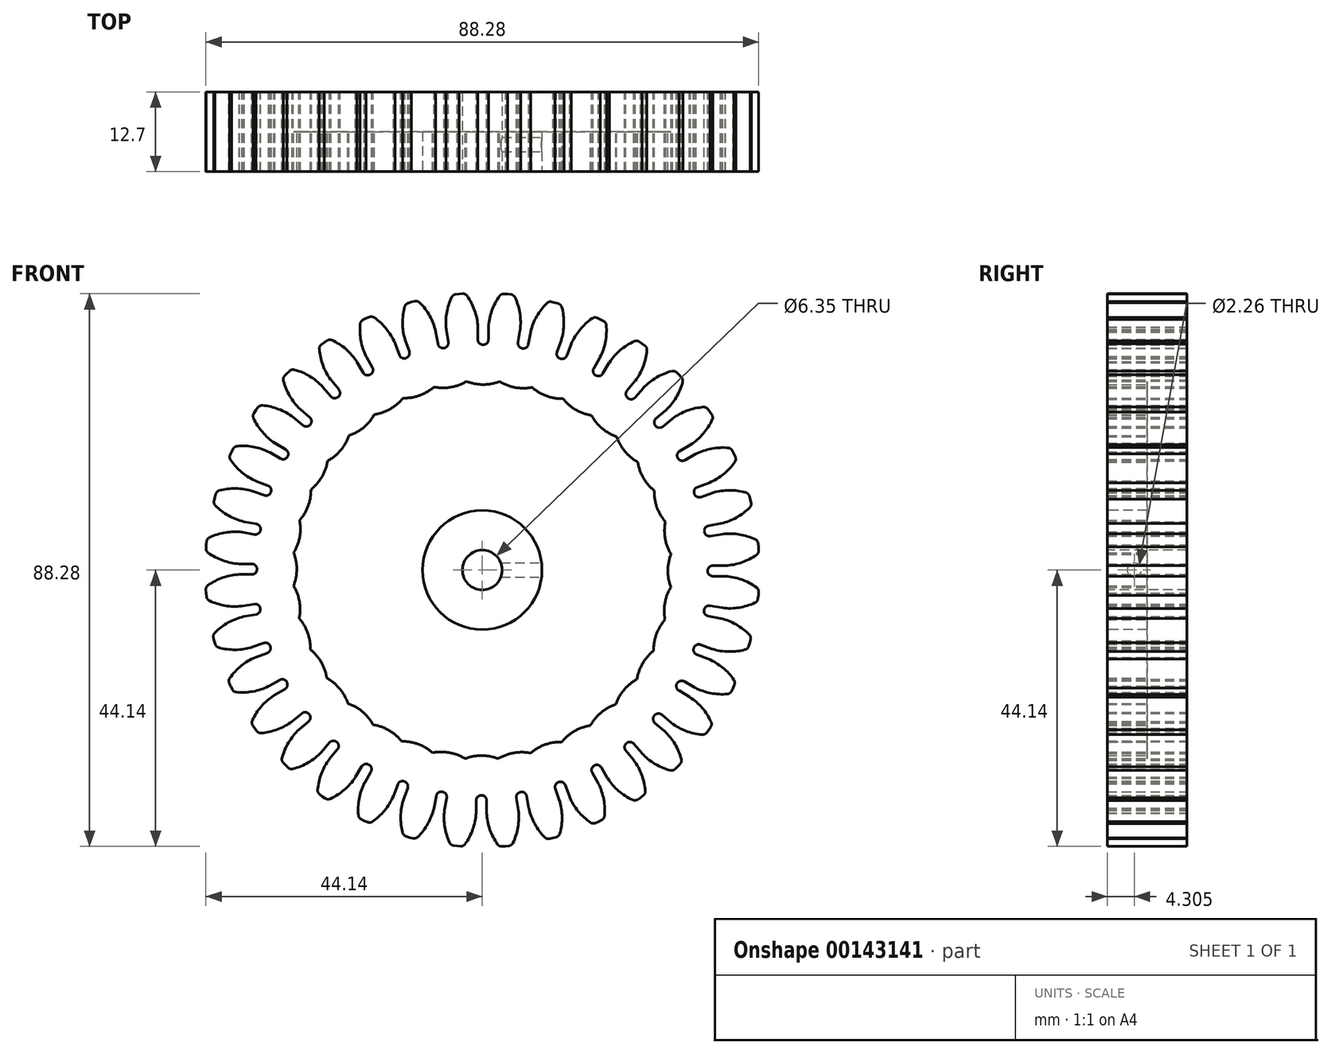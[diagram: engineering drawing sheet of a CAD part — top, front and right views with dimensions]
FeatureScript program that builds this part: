
annotation { "Feature Type Name" : "Feature", "Feature Type Description" : "" }
export const myFeature = defineFeature(function(context is Context, id is Id, definition is map)
    precondition{}
    {
        {
            var Q0;
            Q0=qCreatedBy(makeId("Front.planeOp"),FACE);
            var sketch = newSketch(context, id + "F0", { "sketchPlane" : qUnion([Q0])});
            skArc(sketch, "E0.trimOffspring", {"start": v(-0.7, 38.83) * mm, "mid": v(-1.22, 41.43) * mm, "end": v(-2.42, 43.78) * mm});
            skLineSegment(sketch, "E1", {"start": v(-3.13, 44.14) * mm, "end": v(-3.7, 44.11) * mm});
            skLineSegment(sketch, "E2", {"start": v(-0.7, 38.79) * mm, "end": v(-0.7, 36.8) * mm});
            skArc(sketch, "E3.filletArc", {"start": v(-0.7, 36.8) * mm, "mid": v(-0.46, 36.22) * mm, "end": v(0.12, 35.98) * mm});
            skArc(sketch, "E4.filletArc", {"start": v(-2.42, 43.78) * mm, "mid": v(-2.73, 44.05) * mm, "end": v(-3.13, 44.14) * mm});
            skArc(sketch, "E5.filletArc", {"start": v(-0.7, 38.79) * mm, "mid": v(-0.7, 38.8) * mm, "end": v(-0.7, 38.83) * mm});
            skLineSegment(sketch, "E6.MirrorCS", {"start": v(-4.25, 44.04) * mm, "end": v(-3.7, 44.11) * mm});
            skArc(sketch, "E7.MirrorCS", {"start": v(-4.9, 43.58) * mm, "mid": v(-4.63, 43.9) * mm, "end": v(-4.25, 44.04) * mm});
            skArc(sketch, "E8.MirrorCS", {"start": v(-5.76, 38.4) * mm, "mid": v(-5.69, 41.05) * mm, "end": v(-4.9, 43.58) * mm});
            skLineSegment(sketch, "E9.MirrorCS", {"start": v(-5.75, 38.36) * mm, "end": v(-5.42, 36.4) * mm});
            skArc(sketch, "E10.MirrorCS", {"start": v(-5.42, 36.4) * mm, "mid": v(-5.56, 35.8) * mm, "end": v(-6.1, 35.46) * mm});
            skArc(sketch, "E11.1.0", {"start": v(-11.66, 34.91) * mm, "mid": v(-11.7, 34.28) * mm, "end": v(-12.16, 33.86) * mm});
            skLineSegment(sketch, "E11.1.1", {"start": v(-12.33, 36.78) * mm, "end": v(-11.66, 34.91) * mm});
            skArc(sketch, "E11.1.2", {"start": v(-12.34, 36.82) * mm, "mid": v(-12.73, 39.44) * mm, "end": v(-12.39, 42.07) * mm});
            skArc(sketch, "E11.1.3", {"start": v(-12.39, 42.07) * mm, "mid": v(-12.18, 42.42) * mm, "end": v(-11.83, 42.63) * mm});
            skLineSegment(sketch, "E11.1.4", {"start": v(-11.83, 42.63) * mm, "end": v(-11.3, 42.8) * mm});
            skLineSegment(sketch, "E11.1.5", {"start": v(-10.75, 42.92) * mm, "end": v(-11.3, 42.8) * mm});
            skArc(sketch, "E11.1.6", {"start": v(-9.99, 42.7) * mm, "mid": v(-10.34, 42.9) * mm, "end": v(-10.75, 42.92) * mm});
            skArc(sketch, "E11.1.7", {"start": v(-7.44, 38.12) * mm, "mid": v(-8.4, 40.59) * mm, "end": v(-9.99, 42.7) * mm});
            skLineSegment(sketch, "E11.1.8", {"start": v(-7.43, 38.07) * mm, "end": v(-7.09, 36.12) * mm});
            skArc(sketch, "E11.1.9", {"start": v(-7.09, 36.12) * mm, "mid": v(-6.75, 35.6) * mm, "end": v(-6.13, 35.45) * mm});
            skArc(sketch, "E11.2.0", {"start": v(-17.55, 32.36) * mm, "mid": v(-17.47, 31.73) * mm, "end": v(-17.86, 31.23) * mm});
            skLineSegment(sketch, "E11.2.1", {"start": v(-18.53, 34.08) * mm, "end": v(-17.55, 32.36) * mm});
            skArc(sketch, "E11.2.2", {"start": v(-18.55, 34.12) * mm, "mid": v(-19.39, 36.63) * mm, "end": v(-19.5, 39.28) * mm});
            skArc(sketch, "E11.2.3", {"start": v(-19.5, 39.28) * mm, "mid": v(-19.36, 39.66) * mm, "end": v(-19.06, 39.93) * mm});
            skLineSegment(sketch, "E11.2.4", {"start": v(-19.06, 39.93) * mm, "end": v(-18.56, 40.19) * mm});
            skLineSegment(sketch, "E11.2.5", {"start": v(-18.04, 40.4) * mm, "end": v(-18.56, 40.19) * mm});
            skArc(sketch, "E11.2.6", {"start": v(-17.25, 40.32) * mm, "mid": v(-17.63, 40.46) * mm, "end": v(-18.04, 40.4) * mm});
            skArc(sketch, "E11.2.7", {"start": v(-13.95, 36.25) * mm, "mid": v(-15.31, 38.51) * mm, "end": v(-17.25, 40.32) * mm});
            skLineSegment(sketch, "E11.2.8", {"start": v(-13.93, 36.2) * mm, "end": v(-13.25, 34.34) * mm});
            skArc(sketch, "E11.2.9", {"start": v(-13.25, 34.34) * mm, "mid": v(-12.83, 33.88) * mm, "end": v(-12.2, 33.85) * mm});
            skArc(sketch, "E11.3.0", {"start": v(-22.9, 28.82) * mm, "mid": v(-22.72, 28.22) * mm, "end": v(-23.01, 27.66) * mm});
            skLineSegment(sketch, "E11.3.1", {"start": v(-24.16, 30.35) * mm, "end": v(-22.9, 28.82) * mm});
            skArc(sketch, "E11.3.2", {"start": v(-24.2, 30.38) * mm, "mid": v(-25.45, 32.7) * mm, "end": v(-26.03, 35.3) * mm});
            skArc(sketch, "E11.3.3", {"start": v(-26.03, 35.3) * mm, "mid": v(-25.96, 35.7) * mm, "end": v(-25.7, 36.02) * mm});
            skLineSegment(sketch, "E11.3.4", {"start": v(-25.7, 36.02) * mm, "end": v(-25.25, 36.35) * mm});
            skLineSegment(sketch, "E11.3.5", {"start": v(-24.78, 36.66) * mm, "end": v(-25.25, 36.36) * mm});
            skArc(sketch, "E11.3.6", {"start": v(-23.99, 36.7) * mm, "mid": v(-24.4, 36.78) * mm, "end": v(-24.78, 36.66) * mm});
            skArc(sketch, "E11.3.7", {"start": v(-20.03, 33.28) * mm, "mid": v(-21.77, 35.27) * mm, "end": v(-23.99, 36.7) * mm});
            skLineSegment(sketch, "E11.3.8", {"start": v(-20, 33.24) * mm, "end": v(-19.01, 31.52) * mm});
            skArc(sketch, "E11.3.9", {"start": v(-19.01, 31.52) * mm, "mid": v(-18.51, 31.14) * mm, "end": v(-17.89, 31.22) * mm});
            skArc(sketch, "E11.4.0", {"start": v(-27.56, 24.4) * mm, "mid": v(-27.27, 23.84) * mm, "end": v(-27.46, 23.24) * mm});
            skLineSegment(sketch, "E11.4.1", {"start": v(-29.07, 25.69) * mm, "end": v(-27.56, 24.4) * mm});
            skArc(sketch, "E11.4.2", {"start": v(-29.1, 25.72) * mm, "mid": v(-30.75, 27.8) * mm, "end": v(-31.76, 30.24) * mm});
            skArc(sketch, "E11.4.3", {"start": v(-31.76, 30.24) * mm, "mid": v(-31.76, 30.65) * mm, "end": v(-31.57, 31) * mm});
            skLineSegment(sketch, "E11.4.4", {"start": v(-31.57, 31) * mm, "end": v(-31.18, 31.42) * mm});
            skLineSegment(sketch, "E11.4.5", {"start": v(-30.77, 31.8) * mm, "end": v(-31.18, 31.42) * mm});
            skArc(sketch, "E11.4.6", {"start": v(-30, 31.99) * mm, "mid": v(-30.4, 31.99) * mm, "end": v(-30.77, 31.8) * mm});
            skArc(sketch, "E11.4.7", {"start": v(-25.5, 29.3) * mm, "mid": v(-27.56, 30.95) * mm, "end": v(-30, 31.99) * mm});
            skLineSegment(sketch, "E11.4.8", {"start": v(-25.47, 29.26) * mm, "end": v(-24.2, 27.74) * mm});
            skArc(sketch, "E11.4.9", {"start": v(-24.2, 27.74) * mm, "mid": v(-23.64, 27.45) * mm, "end": v(-23.04, 27.64) * mm});
            skArc(sketch, "E11.5.0", {"start": v(-31.38, 19.25) * mm, "mid": v(-31, 18.75) * mm, "end": v(-31.08, 18.12) * mm});
            skLineSegment(sketch, "E11.5.1", {"start": v(-33.09, 20.25) * mm, "end": v(-31.38, 19.25) * mm});
            skArc(sketch, "E11.5.2", {"start": v(-33.12, 20.28) * mm, "mid": v(-35.1, 22.03) * mm, "end": v(-36.53, 24.26) * mm});
            skArc(sketch, "E11.5.3", {"start": v(-36.53, 24.26) * mm, "mid": v(-36.6, 24.67) * mm, "end": v(-36.47, 25.05) * mm});
            skLineSegment(sketch, "E11.5.4", {"start": v(-36.47, 25.05) * mm, "end": v(-36.17, 25.52) * mm});
            skLineSegment(sketch, "E11.5.5", {"start": v(-35.82, 25.97) * mm, "end": v(-36.16, 25.53) * mm});
            skArc(sketch, "E11.5.6", {"start": v(-35.1, 26.29) * mm, "mid": v(-35.5, 26.22) * mm, "end": v(-35.82, 25.97) * mm});
            skArc(sketch, "E11.5.7", {"start": v(-30.2, 24.42) * mm, "mid": v(-32.52, 25.7) * mm, "end": v(-35.1, 26.29) * mm});
            skLineSegment(sketch, "E11.5.8", {"start": v(-30.17, 24.4) * mm, "end": v(-28.65, 23.12) * mm});
            skArc(sketch, "E11.5.9", {"start": v(-28.65, 23.12) * mm, "mid": v(-28.05, 22.93) * mm, "end": v(-27.49, 23.22) * mm});
            skArc(sketch, "E11.6.0", {"start": v(-34.24, 13.5) * mm, "mid": v(-33.78, 13.08) * mm, "end": v(-33.76, 12.45) * mm});
            skLineSegment(sketch, "E11.6.1", {"start": v(-36.1, 14.2) * mm, "end": v(-34.24, 13.5) * mm});
            skArc(sketch, "E11.6.2", {"start": v(-36.14, 14.22) * mm, "mid": v(-38.4, 15.6) * mm, "end": v(-40.19, 17.55) * mm});
            skArc(sketch, "E11.6.3", {"start": v(-40.19, 17.55) * mm, "mid": v(-40.33, 17.94) * mm, "end": v(-40.27, 18.34) * mm});
            skLineSegment(sketch, "E11.6.4", {"start": v(-40.27, 18.34) * mm, "end": v(-40.05, 18.86) * mm});
            skLineSegment(sketch, "E11.6.5", {"start": v(-39.79, 19.35) * mm, "end": v(-40.05, 18.86) * mm});
            skArc(sketch, "E11.6.6", {"start": v(-39.13, 19.8) * mm, "mid": v(-39.52, 19.66) * mm, "end": v(-39.79, 19.35) * mm});
            skArc(sketch, "E11.6.7", {"start": v(-33.98, 18.8) * mm, "mid": v(-36.49, 19.66) * mm, "end": v(-39.13, 19.8) * mm});
            skLineSegment(sketch, "E11.6.8", {"start": v(-33.94, 18.78) * mm, "end": v(-32.23, 17.8) * mm});
            skArc(sketch, "E11.6.9", {"start": v(-32.23, 17.8) * mm, "mid": v(-31.6, 17.7) * mm, "end": v(-31.1, 18.1) * mm});
            skArc(sketch, "E11.7.0", {"start": v(-36.07, 7.36) * mm, "mid": v(-35.54, 7.01) * mm, "end": v(-35.4, 6.4) * mm});
            skLineSegment(sketch, "E11.7.1", {"start": v(-38.02, 7.71) * mm, "end": v(-36.07, 7.36) * mm});
            skArc(sketch, "E11.7.2", {"start": v(-38.06, 7.72) * mm, "mid": v(-40.52, 8.7) * mm, "end": v(-42.62, 10.3) * mm});
            skArc(sketch, "E11.7.3", {"start": v(-42.62, 10.3) * mm, "mid": v(-42.83, 10.66) * mm, "end": v(-42.84, 11.07) * mm});
            skLineSegment(sketch, "E11.7.4", {"start": v(-42.84, 11.07) * mm, "end": v(-42.71, 11.62) * mm});
            skLineSegment(sketch, "E11.7.5", {"start": v(-42.54, 12.15) * mm, "end": v(-42.71, 11.62) * mm});
            skArc(sketch, "E11.7.6", {"start": v(-41.97, 12.7) * mm, "mid": v(-42.33, 12.5) * mm, "end": v(-42.54, 12.15) * mm});
            skArc(sketch, "E11.7.7", {"start": v(-36.73, 12.62) * mm, "mid": v(-39.35, 13.03) * mm, "end": v(-41.97, 12.7) * mm});
            skLineSegment(sketch, "E11.7.8", {"start": v(-36.69, 12.6) * mm, "end": v(-34.83, 11.92) * mm});
            skArc(sketch, "E11.7.9", {"start": v(-34.83, 11.92) * mm, "mid": v(-34.2, 11.95) * mm, "end": v(-33.77, 12.42) * mm});
            skArc(sketch, "E11.8.0", {"start": v(-36.8, 0.98) * mm, "mid": v(-36.22, 0.74) * mm, "end": v(-35.98, 0.15) * mm});
            skLineSegment(sketch, "E11.8.1", {"start": v(-38.78, 1) * mm, "end": v(-36.8, 0.98) * mm});
            skArc(sketch, "E11.8.2", {"start": v(-38.82, 1) * mm, "mid": v(-41.42, 1.53) * mm, "end": v(-43.77, 2.75) * mm});
            skArc(sketch, "E11.8.3", {"start": v(-43.77, 2.75) * mm, "mid": v(-44.03, 3.06) * mm, "end": v(-44.11, 3.46) * mm});
            skLineSegment(sketch, "E11.8.4", {"start": v(-44.11, 3.46) * mm, "end": v(-44.08, 4.02) * mm});
            skLineSegment(sketch, "E11.8.5", {"start": v(-44, 4.58) * mm, "end": v(-44.08, 4.02) * mm});
            skArc(sketch, "E11.8.6", {"start": v(-43.54, 5.22) * mm, "mid": v(-43.86, 4.96) * mm, "end": v(-44, 4.58) * mm});
            skArc(sketch, "E11.8.7", {"start": v(-38.36, 6.05) * mm, "mid": v(-41, 6) * mm, "end": v(-43.54, 5.22) * mm});
            skLineSegment(sketch, "E11.8.8", {"start": v(-38.32, 6.04) * mm, "end": v(-36.37, 5.7) * mm});
            skArc(sketch, "E11.8.9", {"start": v(-36.37, 5.7) * mm, "mid": v(-35.75, 5.83) * mm, "end": v(-35.41, 6.36) * mm});
            skArc(sketch, "E11.9.0", {"start": v(-36.4, -5.42) * mm, "mid": v(-35.8, -5.56) * mm, "end": v(-35.46, -6.1) * mm});
            skLineSegment(sketch, "E11.9.1", {"start": v(-38.36, -5.75) * mm, "end": v(-36.4, -5.42) * mm});
            skArc(sketch, "E11.9.2", {"start": v(-38.4, -5.76) * mm, "mid": v(-41.05, -5.69) * mm, "end": v(-43.58, -4.9) * mm});
            skArc(sketch, "E11.9.3", {"start": v(-43.58, -4.9) * mm, "mid": v(-43.9, -4.63) * mm, "end": v(-44.04, -4.25) * mm});
            skLineSegment(sketch, "E11.9.4", {"start": v(-44.04, -4.25) * mm, "end": v(-44.11, -3.7) * mm});
            skLineSegment(sketch, "E11.9.5", {"start": v(-44.14, -3.13) * mm, "end": v(-44.11, -3.7) * mm});
            skArc(sketch, "E11.9.6", {"start": v(-43.78, -2.42) * mm, "mid": v(-44.05, -2.73) * mm, "end": v(-44.14, -3.13) * mm});
            skArc(sketch, "E11.9.7", {"start": v(-38.83, -0.7) * mm, "mid": v(-41.43, -1.22) * mm, "end": v(-43.78, -2.42) * mm});
            skLineSegment(sketch, "E11.9.8", {"start": v(-38.79, -0.7) * mm, "end": v(-36.8, -0.7) * mm});
            skArc(sketch, "E11.9.9", {"start": v(-36.8, -0.7) * mm, "mid": v(-36.22, -0.46) * mm, "end": v(-35.98, 0.12) * mm});
            skArc(sketch, "E11.10.0", {"start": v(-34.91, -11.66) * mm, "mid": v(-34.28, -11.7) * mm, "end": v(-33.86, -12.16) * mm});
            skLineSegment(sketch, "E11.10.1", {"start": v(-36.78, -12.33) * mm, "end": v(-34.91, -11.66) * mm});
            skArc(sketch, "E11.10.2", {"start": v(-36.82, -12.34) * mm, "mid": v(-39.44, -12.73) * mm, "end": v(-42.07, -12.39) * mm});
            skArc(sketch, "E11.10.3", {"start": v(-42.07, -12.39) * mm, "mid": v(-42.42, -12.18) * mm, "end": v(-42.63, -11.83) * mm});
            skLineSegment(sketch, "E11.10.4", {"start": v(-42.63, -11.83) * mm, "end": v(-42.8, -11.3) * mm});
            skLineSegment(sketch, "E11.10.5", {"start": v(-42.92, -10.75) * mm, "end": v(-42.8, -11.3) * mm});
            skArc(sketch, "E11.10.6", {"start": v(-42.7, -9.99) * mm, "mid": v(-42.9, -10.34) * mm, "end": v(-42.92, -10.75) * mm});
            skArc(sketch, "E11.10.7", {"start": v(-38.12, -7.44) * mm, "mid": v(-40.59, -8.4) * mm, "end": v(-42.7, -9.99) * mm});
            skLineSegment(sketch, "E11.10.8", {"start": v(-38.07, -7.43) * mm, "end": v(-36.12, -7.09) * mm});
            skArc(sketch, "E11.10.9", {"start": v(-36.12, -7.09) * mm, "mid": v(-35.6, -6.75) * mm, "end": v(-35.45, -6.13) * mm});
            skArc(sketch, "E11.11.0", {"start": v(-32.36, -17.55) * mm, "mid": v(-31.73, -17.47) * mm, "end": v(-31.23, -17.86) * mm});
            skLineSegment(sketch, "E11.11.1", {"start": v(-34.08, -18.53) * mm, "end": v(-32.36, -17.55) * mm});
            skArc(sketch, "E11.11.2", {"start": v(-34.12, -18.55) * mm, "mid": v(-36.63, -19.39) * mm, "end": v(-39.28, -19.5) * mm});
            skArc(sketch, "E11.11.3", {"start": v(-39.28, -19.5) * mm, "mid": v(-39.66, -19.36) * mm, "end": v(-39.93, -19.06) * mm});
            skLineSegment(sketch, "E11.11.4", {"start": v(-39.93, -19.06) * mm, "end": v(-40.19, -18.56) * mm});
            skLineSegment(sketch, "E11.11.5", {"start": v(-40.4, -18.04) * mm, "end": v(-40.19, -18.56) * mm});
            skArc(sketch, "E11.11.6", {"start": v(-40.32, -17.25) * mm, "mid": v(-40.46, -17.63) * mm, "end": v(-40.4, -18.04) * mm});
            skArc(sketch, "E11.11.7", {"start": v(-36.25, -13.95) * mm, "mid": v(-38.51, -15.31) * mm, "end": v(-40.32, -17.25) * mm});
            skLineSegment(sketch, "E11.11.8", {"start": v(-36.2, -13.93) * mm, "end": v(-34.34, -13.25) * mm});
            skArc(sketch, "E11.11.9", {"start": v(-34.34, -13.25) * mm, "mid": v(-33.88, -12.83) * mm, "end": v(-33.85, -12.2) * mm});
            skArc(sketch, "E11.12.0", {"start": v(-28.82, -22.9) * mm, "mid": v(-28.22, -22.72) * mm, "end": v(-27.66, -23.01) * mm});
            skLineSegment(sketch, "E11.12.1", {"start": v(-30.35, -24.16) * mm, "end": v(-28.82, -22.9) * mm});
            skArc(sketch, "E11.12.2", {"start": v(-30.38, -24.2) * mm, "mid": v(-32.7, -25.45) * mm, "end": v(-35.3, -26.03) * mm});
            skArc(sketch, "E11.12.3", {"start": v(-35.3, -26.03) * mm, "mid": v(-35.7, -25.96) * mm, "end": v(-36.02, -25.7) * mm});
            skLineSegment(sketch, "E11.12.4", {"start": v(-36.02, -25.7) * mm, "end": v(-36.35, -25.25) * mm});
            skLineSegment(sketch, "E11.12.5", {"start": v(-36.66, -24.78) * mm, "end": v(-36.36, -25.25) * mm});
            skArc(sketch, "E11.12.6", {"start": v(-36.7, -23.99) * mm, "mid": v(-36.78, -24.4) * mm, "end": v(-36.66, -24.78) * mm});
            skArc(sketch, "E11.12.7", {"start": v(-33.28, -20.03) * mm, "mid": v(-35.27, -21.77) * mm, "end": v(-36.7, -23.99) * mm});
            skLineSegment(sketch, "E11.12.8", {"start": v(-33.24, -20) * mm, "end": v(-31.52, -19.01) * mm});
            skArc(sketch, "E11.12.9", {"start": v(-31.52, -19.01) * mm, "mid": v(-31.14, -18.51) * mm, "end": v(-31.22, -17.89) * mm});
            skArc(sketch, "E11.13.0", {"start": v(-24.4, -27.56) * mm, "mid": v(-23.84, -27.27) * mm, "end": v(-23.24, -27.46) * mm});
            skLineSegment(sketch, "E11.13.1", {"start": v(-25.69, -29.07) * mm, "end": v(-24.4, -27.56) * mm});
            skArc(sketch, "E11.13.2", {"start": v(-25.72, -29.1) * mm, "mid": v(-27.8, -30.75) * mm, "end": v(-30.24, -31.76) * mm});
            skArc(sketch, "E11.13.3", {"start": v(-30.24, -31.76) * mm, "mid": v(-30.65, -31.76) * mm, "end": v(-31, -31.57) * mm});
            skLineSegment(sketch, "E11.13.4", {"start": v(-31, -31.57) * mm, "end": v(-31.42, -31.18) * mm});
            skLineSegment(sketch, "E11.13.5", {"start": v(-31.8, -30.77) * mm, "end": v(-31.42, -31.18) * mm});
            skArc(sketch, "E11.13.6", {"start": v(-31.99, -30) * mm, "mid": v(-31.99, -30.4) * mm, "end": v(-31.8, -30.77) * mm});
            skArc(sketch, "E11.13.7", {"start": v(-29.3, -25.5) * mm, "mid": v(-30.95, -27.56) * mm, "end": v(-31.99, -30) * mm});
            skLineSegment(sketch, "E11.13.8", {"start": v(-29.26, -25.47) * mm, "end": v(-27.74, -24.2) * mm});
            skArc(sketch, "E11.13.9", {"start": v(-27.74, -24.2) * mm, "mid": v(-27.45, -23.64) * mm, "end": v(-27.64, -23.04) * mm});
            skArc(sketch, "E11.14.0", {"start": v(-19.25, -31.38) * mm, "mid": v(-18.75, -31) * mm, "end": v(-18.12, -31.08) * mm});
            skLineSegment(sketch, "E11.14.1", {"start": v(-20.25, -33.09) * mm, "end": v(-19.25, -31.38) * mm});
            skArc(sketch, "E11.14.2", {"start": v(-20.28, -33.12) * mm, "mid": v(-22.03, -35.1) * mm, "end": v(-24.26, -36.53) * mm});
            skArc(sketch, "E11.14.3", {"start": v(-24.26, -36.53) * mm, "mid": v(-24.67, -36.6) * mm, "end": v(-25.05, -36.47) * mm});
            skLineSegment(sketch, "E11.14.4", {"start": v(-25.05, -36.47) * mm, "end": v(-25.52, -36.17) * mm});
            skLineSegment(sketch, "E11.14.5", {"start": v(-25.97, -35.82) * mm, "end": v(-25.53, -36.16) * mm});
            skArc(sketch, "E11.14.6", {"start": v(-26.29, -35.1) * mm, "mid": v(-26.22, -35.5) * mm, "end": v(-25.97, -35.82) * mm});
            skArc(sketch, "E11.14.7", {"start": v(-24.42, -30.2) * mm, "mid": v(-25.7, -32.52) * mm, "end": v(-26.29, -35.1) * mm});
            skLineSegment(sketch, "E11.14.8", {"start": v(-24.4, -30.17) * mm, "end": v(-23.12, -28.65) * mm});
            skArc(sketch, "E11.14.9", {"start": v(-23.12, -28.65) * mm, "mid": v(-22.93, -28.05) * mm, "end": v(-23.22, -27.49) * mm});
            skArc(sketch, "E11.15.0", {"start": v(-13.5, -34.24) * mm, "mid": v(-13.08, -33.78) * mm, "end": v(-12.45, -33.76) * mm});
            skLineSegment(sketch, "E11.15.1", {"start": v(-14.2, -36.1) * mm, "end": v(-13.5, -34.24) * mm});
            skArc(sketch, "E11.15.2", {"start": v(-14.22, -36.14) * mm, "mid": v(-15.6, -38.4) * mm, "end": v(-17.55, -40.19) * mm});
            skArc(sketch, "E11.15.3", {"start": v(-17.55, -40.19) * mm, "mid": v(-17.94, -40.33) * mm, "end": v(-18.34, -40.27) * mm});
            skLineSegment(sketch, "E11.15.4", {"start": v(-18.34, -40.27) * mm, "end": v(-18.86, -40.05) * mm});
            skLineSegment(sketch, "E11.15.5", {"start": v(-19.35, -39.79) * mm, "end": v(-18.86, -40.05) * mm});
            skArc(sketch, "E11.15.6", {"start": v(-19.8, -39.13) * mm, "mid": v(-19.66, -39.52) * mm, "end": v(-19.35, -39.79) * mm});
            skArc(sketch, "E11.15.7", {"start": v(-18.8, -33.98) * mm, "mid": v(-19.66, -36.49) * mm, "end": v(-19.8, -39.13) * mm});
            skLineSegment(sketch, "E11.15.8", {"start": v(-18.78, -33.94) * mm, "end": v(-17.8, -32.23) * mm});
            skArc(sketch, "E11.15.9", {"start": v(-17.8, -32.23) * mm, "mid": v(-17.7, -31.6) * mm, "end": v(-18.1, -31.1) * mm});
            skArc(sketch, "E11.16.0", {"start": v(-7.36, -36.07) * mm, "mid": v(-7.01, -35.54) * mm, "end": v(-6.4, -35.4) * mm});
            skLineSegment(sketch, "E11.16.1", {"start": v(-7.71, -38.02) * mm, "end": v(-7.36, -36.07) * mm});
            skArc(sketch, "E11.16.2", {"start": v(-7.72, -38.06) * mm, "mid": v(-8.7, -40.52) * mm, "end": v(-10.3, -42.62) * mm});
            skArc(sketch, "E11.16.3", {"start": v(-10.3, -42.62) * mm, "mid": v(-10.66, -42.83) * mm, "end": v(-11.07, -42.84) * mm});
            skLineSegment(sketch, "E11.16.4", {"start": v(-11.07, -42.84) * mm, "end": v(-11.62, -42.71) * mm});
            skLineSegment(sketch, "E11.16.5", {"start": v(-12.15, -42.54) * mm, "end": v(-11.62, -42.71) * mm});
            skArc(sketch, "E11.16.6", {"start": v(-12.7, -41.97) * mm, "mid": v(-12.5, -42.33) * mm, "end": v(-12.15, -42.54) * mm});
            skArc(sketch, "E11.16.7", {"start": v(-12.62, -36.73) * mm, "mid": v(-13.03, -39.35) * mm, "end": v(-12.7, -41.97) * mm});
            skLineSegment(sketch, "E11.16.8", {"start": v(-12.6, -36.69) * mm, "end": v(-11.92, -34.83) * mm});
            skArc(sketch, "E11.16.9", {"start": v(-11.92, -34.83) * mm, "mid": v(-11.95, -34.2) * mm, "end": v(-12.42, -33.77) * mm});
            skArc(sketch, "E11.17.0", {"start": v(-0.98, -36.8) * mm, "mid": v(-0.74, -36.22) * mm, "end": v(-0.15, -35.98) * mm});
            skLineSegment(sketch, "E11.17.1", {"start": v(-1, -38.78) * mm, "end": v(-0.98, -36.8) * mm});
            skArc(sketch, "E11.17.2", {"start": v(-1, -38.82) * mm, "mid": v(-1.53, -41.42) * mm, "end": v(-2.75, -43.77) * mm});
            skArc(sketch, "E11.17.3", {"start": v(-2.75, -43.77) * mm, "mid": v(-3.06, -44.03) * mm, "end": v(-3.46, -44.11) * mm});
            skLineSegment(sketch, "E11.17.4", {"start": v(-3.46, -44.11) * mm, "end": v(-4.02, -44.08) * mm});
            skLineSegment(sketch, "E11.17.5", {"start": v(-4.58, -44) * mm, "end": v(-4.02, -44.08) * mm});
            skArc(sketch, "E11.17.6", {"start": v(-5.22, -43.54) * mm, "mid": v(-4.96, -43.86) * mm, "end": v(-4.58, -44) * mm});
            skArc(sketch, "E11.17.7", {"start": v(-6.05, -38.36) * mm, "mid": v(-6, -41) * mm, "end": v(-5.22, -43.54) * mm});
            skLineSegment(sketch, "E11.17.8", {"start": v(-6.04, -38.32) * mm, "end": v(-5.7, -36.37) * mm});
            skArc(sketch, "E11.17.9", {"start": v(-5.7, -36.37) * mm, "mid": v(-5.83, -35.75) * mm, "end": v(-6.36, -35.41) * mm});
            skArc(sketch, "E11.18.0", {"start": v(5.42, -36.4) * mm, "mid": v(5.56, -35.8) * mm, "end": v(6.1, -35.46) * mm});
            skLineSegment(sketch, "E11.18.1", {"start": v(5.75, -38.36) * mm, "end": v(5.42, -36.4) * mm});
            skArc(sketch, "E11.18.2", {"start": v(5.76, -38.4) * mm, "mid": v(5.69, -41.05) * mm, "end": v(4.9, -43.58) * mm});
            skArc(sketch, "E11.18.3", {"start": v(4.9, -43.58) * mm, "mid": v(4.63, -43.9) * mm, "end": v(4.25, -44.04) * mm});
            skLineSegment(sketch, "E11.18.4", {"start": v(4.25, -44.04) * mm, "end": v(3.7, -44.11) * mm});
            skLineSegment(sketch, "E11.18.5", {"start": v(3.13, -44.14) * mm, "end": v(3.7, -44.11) * mm});
            skArc(sketch, "E11.18.6", {"start": v(2.42, -43.78) * mm, "mid": v(2.73, -44.05) * mm, "end": v(3.13, -44.14) * mm});
            skArc(sketch, "E11.18.7", {"start": v(0.7, -38.83) * mm, "mid": v(1.22, -41.43) * mm, "end": v(2.42, -43.78) * mm});
            skLineSegment(sketch, "E11.18.8", {"start": v(0.7, -38.79) * mm, "end": v(0.7, -36.8) * mm});
            skArc(sketch, "E11.18.9", {"start": v(0.7, -36.8) * mm, "mid": v(0.46, -36.22) * mm, "end": v(-0.12, -35.98) * mm});
            skArc(sketch, "E11.19.0", {"start": v(11.66, -34.91) * mm, "mid": v(11.7, -34.28) * mm, "end": v(12.16, -33.86) * mm});
            skLineSegment(sketch, "E11.19.1", {"start": v(12.33, -36.78) * mm, "end": v(11.66, -34.91) * mm});
            skArc(sketch, "E11.19.2", {"start": v(12.34, -36.82) * mm, "mid": v(12.73, -39.44) * mm, "end": v(12.39, -42.07) * mm});
            skArc(sketch, "E11.19.3", {"start": v(12.39, -42.07) * mm, "mid": v(12.18, -42.42) * mm, "end": v(11.83, -42.63) * mm});
            skLineSegment(sketch, "E11.19.4", {"start": v(11.83, -42.63) * mm, "end": v(11.3, -42.8) * mm});
            skLineSegment(sketch, "E11.19.5", {"start": v(10.75, -42.92) * mm, "end": v(11.3, -42.8) * mm});
            skArc(sketch, "E11.19.6", {"start": v(9.99, -42.7) * mm, "mid": v(10.34, -42.9) * mm, "end": v(10.75, -42.92) * mm});
            skArc(sketch, "E11.19.7", {"start": v(7.44, -38.12) * mm, "mid": v(8.4, -40.59) * mm, "end": v(9.99, -42.7) * mm});
            skLineSegment(sketch, "E11.19.8", {"start": v(7.43, -38.07) * mm, "end": v(7.09, -36.12) * mm});
            skArc(sketch, "E11.19.9", {"start": v(7.09, -36.12) * mm, "mid": v(6.75, -35.6) * mm, "end": v(6.13, -35.45) * mm});
            skArc(sketch, "E11.20.0", {"start": v(17.55, -32.36) * mm, "mid": v(17.47, -31.73) * mm, "end": v(17.86, -31.23) * mm});
            skLineSegment(sketch, "E11.20.1", {"start": v(18.53, -34.08) * mm, "end": v(17.55, -32.36) * mm});
            skArc(sketch, "E11.20.2", {"start": v(18.55, -34.12) * mm, "mid": v(19.39, -36.63) * mm, "end": v(19.5, -39.28) * mm});
            skArc(sketch, "E11.20.3", {"start": v(19.5, -39.28) * mm, "mid": v(19.36, -39.66) * mm, "end": v(19.06, -39.93) * mm});
            skLineSegment(sketch, "E11.20.4", {"start": v(19.06, -39.93) * mm, "end": v(18.56, -40.19) * mm});
            skLineSegment(sketch, "E11.20.5", {"start": v(18.04, -40.4) * mm, "end": v(18.56, -40.19) * mm});
            skArc(sketch, "E11.20.6", {"start": v(17.25, -40.32) * mm, "mid": v(17.63, -40.46) * mm, "end": v(18.04, -40.4) * mm});
            skArc(sketch, "E11.20.7", {"start": v(13.95, -36.25) * mm, "mid": v(15.31, -38.51) * mm, "end": v(17.25, -40.32) * mm});
            skLineSegment(sketch, "E11.20.8", {"start": v(13.93, -36.2) * mm, "end": v(13.25, -34.34) * mm});
            skArc(sketch, "E11.20.9", {"start": v(13.25, -34.34) * mm, "mid": v(12.83, -33.88) * mm, "end": v(12.2, -33.85) * mm});
            skArc(sketch, "E11.21.0", {"start": v(22.9, -28.82) * mm, "mid": v(22.72, -28.22) * mm, "end": v(23.01, -27.66) * mm});
            skLineSegment(sketch, "E11.21.1", {"start": v(24.16, -30.35) * mm, "end": v(22.9, -28.82) * mm});
            skArc(sketch, "E11.21.2", {"start": v(24.2, -30.38) * mm, "mid": v(25.45, -32.7) * mm, "end": v(26.03, -35.3) * mm});
            skArc(sketch, "E11.21.3", {"start": v(26.03, -35.3) * mm, "mid": v(25.96, -35.7) * mm, "end": v(25.7, -36.02) * mm});
            skLineSegment(sketch, "E11.21.4", {"start": v(25.7, -36.02) * mm, "end": v(25.25, -36.35) * mm});
            skLineSegment(sketch, "E11.21.5", {"start": v(24.78, -36.66) * mm, "end": v(25.25, -36.36) * mm});
            skArc(sketch, "E11.21.6", {"start": v(23.99, -36.7) * mm, "mid": v(24.4, -36.78) * mm, "end": v(24.78, -36.66) * mm});
            skArc(sketch, "E11.21.7", {"start": v(20.03, -33.28) * mm, "mid": v(21.77, -35.27) * mm, "end": v(23.99, -36.7) * mm});
            skLineSegment(sketch, "E11.21.8", {"start": v(20, -33.24) * mm, "end": v(19.01, -31.52) * mm});
            skArc(sketch, "E11.21.9", {"start": v(19.01, -31.52) * mm, "mid": v(18.51, -31.14) * mm, "end": v(17.89, -31.22) * mm});
            skArc(sketch, "E11.22.0", {"start": v(27.56, -24.4) * mm, "mid": v(27.27, -23.84) * mm, "end": v(27.46, -23.24) * mm});
            skLineSegment(sketch, "E11.22.1", {"start": v(29.07, -25.69) * mm, "end": v(27.56, -24.4) * mm});
            skArc(sketch, "E11.22.2", {"start": v(29.1, -25.72) * mm, "mid": v(30.75, -27.8) * mm, "end": v(31.76, -30.24) * mm});
            skArc(sketch, "E11.22.3", {"start": v(31.76, -30.24) * mm, "mid": v(31.76, -30.65) * mm, "end": v(31.57, -31) * mm});
            skLineSegment(sketch, "E11.22.4", {"start": v(31.57, -31) * mm, "end": v(31.18, -31.42) * mm});
            skLineSegment(sketch, "E11.22.5", {"start": v(30.77, -31.8) * mm, "end": v(31.18, -31.42) * mm});
            skArc(sketch, "E11.22.6", {"start": v(30, -31.99) * mm, "mid": v(30.4, -31.99) * mm, "end": v(30.77, -31.8) * mm});
            skArc(sketch, "E11.22.7", {"start": v(25.5, -29.3) * mm, "mid": v(27.56, -30.95) * mm, "end": v(30, -31.99) * mm});
            skLineSegment(sketch, "E11.22.8", {"start": v(25.47, -29.26) * mm, "end": v(24.2, -27.74) * mm});
            skArc(sketch, "E11.22.9", {"start": v(24.2, -27.74) * mm, "mid": v(23.64, -27.45) * mm, "end": v(23.04, -27.64) * mm});
            skArc(sketch, "E11.23.0", {"start": v(31.38, -19.25) * mm, "mid": v(31, -18.75) * mm, "end": v(31.08, -18.12) * mm});
            skLineSegment(sketch, "E11.23.1", {"start": v(33.09, -20.25) * mm, "end": v(31.38, -19.25) * mm});
            skArc(sketch, "E11.23.2", {"start": v(33.12, -20.28) * mm, "mid": v(35.1, -22.03) * mm, "end": v(36.53, -24.26) * mm});
            skArc(sketch, "E11.23.3", {"start": v(36.53, -24.26) * mm, "mid": v(36.6, -24.67) * mm, "end": v(36.47, -25.05) * mm});
            skLineSegment(sketch, "E11.23.4", {"start": v(36.47, -25.05) * mm, "end": v(36.17, -25.52) * mm});
            skLineSegment(sketch, "E11.23.5", {"start": v(35.82, -25.97) * mm, "end": v(36.16, -25.53) * mm});
            skArc(sketch, "E11.23.6", {"start": v(35.1, -26.29) * mm, "mid": v(35.5, -26.22) * mm, "end": v(35.82, -25.97) * mm});
            skArc(sketch, "E11.23.7", {"start": v(30.2, -24.42) * mm, "mid": v(32.52, -25.7) * mm, "end": v(35.1, -26.29) * mm});
            skLineSegment(sketch, "E11.23.8", {"start": v(30.17, -24.4) * mm, "end": v(28.65, -23.12) * mm});
            skArc(sketch, "E11.23.9", {"start": v(28.65, -23.12) * mm, "mid": v(28.05, -22.93) * mm, "end": v(27.49, -23.22) * mm});
            skArc(sketch, "E11.24.0", {"start": v(34.24, -13.5) * mm, "mid": v(33.78, -13.08) * mm, "end": v(33.76, -12.45) * mm});
            skLineSegment(sketch, "E11.24.1", {"start": v(36.1, -14.2) * mm, "end": v(34.24, -13.5) * mm});
            skArc(sketch, "E11.24.2", {"start": v(36.14, -14.22) * mm, "mid": v(38.4, -15.6) * mm, "end": v(40.19, -17.55) * mm});
            skArc(sketch, "E11.24.3", {"start": v(40.19, -17.55) * mm, "mid": v(40.33, -17.94) * mm, "end": v(40.27, -18.34) * mm});
            skLineSegment(sketch, "E11.24.4", {"start": v(40.27, -18.34) * mm, "end": v(40.05, -18.86) * mm});
            skLineSegment(sketch, "E11.24.5", {"start": v(39.79, -19.35) * mm, "end": v(40.05, -18.86) * mm});
            skArc(sketch, "E11.24.6", {"start": v(39.13, -19.8) * mm, "mid": v(39.52, -19.66) * mm, "end": v(39.79, -19.35) * mm});
            skArc(sketch, "E11.24.7", {"start": v(33.98, -18.8) * mm, "mid": v(36.49, -19.66) * mm, "end": v(39.13, -19.8) * mm});
            skLineSegment(sketch, "E11.24.8", {"start": v(33.94, -18.78) * mm, "end": v(32.23, -17.8) * mm});
            skArc(sketch, "E11.24.9", {"start": v(32.23, -17.8) * mm, "mid": v(31.6, -17.7) * mm, "end": v(31.1, -18.1) * mm});
            skArc(sketch, "E11.25.0", {"start": v(36.07, -7.36) * mm, "mid": v(35.54, -7.01) * mm, "end": v(35.4, -6.4) * mm});
            skLineSegment(sketch, "E11.25.1", {"start": v(38.02, -7.71) * mm, "end": v(36.07, -7.36) * mm});
            skArc(sketch, "E11.25.2", {"start": v(38.06, -7.72) * mm, "mid": v(40.52, -8.7) * mm, "end": v(42.62, -10.3) * mm});
            skArc(sketch, "E11.25.3", {"start": v(42.62, -10.3) * mm, "mid": v(42.83, -10.66) * mm, "end": v(42.84, -11.07) * mm});
            skLineSegment(sketch, "E11.25.4", {"start": v(42.84, -11.07) * mm, "end": v(42.71, -11.62) * mm});
            skLineSegment(sketch, "E11.25.5", {"start": v(42.54, -12.15) * mm, "end": v(42.71, -11.62) * mm});
            skArc(sketch, "E11.25.6", {"start": v(41.97, -12.7) * mm, "mid": v(42.33, -12.5) * mm, "end": v(42.54, -12.15) * mm});
            skArc(sketch, "E11.25.7", {"start": v(36.73, -12.62) * mm, "mid": v(39.35, -13.03) * mm, "end": v(41.97, -12.7) * mm});
            skLineSegment(sketch, "E11.25.8", {"start": v(36.69, -12.6) * mm, "end": v(34.83, -11.92) * mm});
            skArc(sketch, "E11.25.9", {"start": v(34.83, -11.92) * mm, "mid": v(34.2, -11.95) * mm, "end": v(33.77, -12.42) * mm});
            skArc(sketch, "E11.26.0", {"start": v(36.8, -0.98) * mm, "mid": v(36.22, -0.74) * mm, "end": v(35.98, -0.15) * mm});
            skLineSegment(sketch, "E11.26.1", {"start": v(38.78, -1) * mm, "end": v(36.8, -0.98) * mm});
            skArc(sketch, "E11.26.2", {"start": v(38.82, -1) * mm, "mid": v(41.42, -1.53) * mm, "end": v(43.77, -2.75) * mm});
            skArc(sketch, "E11.26.3", {"start": v(43.77, -2.75) * mm, "mid": v(44.03, -3.06) * mm, "end": v(44.11, -3.46) * mm});
            skLineSegment(sketch, "E11.26.4", {"start": v(44.11, -3.46) * mm, "end": v(44.08, -4.02) * mm});
            skLineSegment(sketch, "E11.26.5", {"start": v(44, -4.58) * mm, "end": v(44.08, -4.02) * mm});
            skArc(sketch, "E11.26.6", {"start": v(43.54, -5.22) * mm, "mid": v(43.86, -4.96) * mm, "end": v(44, -4.58) * mm});
            skArc(sketch, "E11.26.7", {"start": v(38.36, -6.05) * mm, "mid": v(41, -6) * mm, "end": v(43.54, -5.22) * mm});
            skLineSegment(sketch, "E11.26.8", {"start": v(38.32, -6.04) * mm, "end": v(36.37, -5.7) * mm});
            skArc(sketch, "E11.26.9", {"start": v(36.37, -5.7) * mm, "mid": v(35.75, -5.83) * mm, "end": v(35.41, -6.36) * mm});
            skArc(sketch, "E11.27.0", {"start": v(36.4, 5.42) * mm, "mid": v(35.8, 5.56) * mm, "end": v(35.46, 6.1) * mm});
            skLineSegment(sketch, "E11.27.1", {"start": v(38.36, 5.75) * mm, "end": v(36.4, 5.42) * mm});
            skArc(sketch, "E11.27.2", {"start": v(38.4, 5.76) * mm, "mid": v(41.05, 5.69) * mm, "end": v(43.58, 4.9) * mm});
            skArc(sketch, "E11.27.3", {"start": v(43.58, 4.9) * mm, "mid": v(43.9, 4.63) * mm, "end": v(44.04, 4.25) * mm});
            skLineSegment(sketch, "E11.27.4", {"start": v(44.04, 4.25) * mm, "end": v(44.11, 3.7) * mm});
            skLineSegment(sketch, "E11.27.5", {"start": v(44.14, 3.13) * mm, "end": v(44.11, 3.7) * mm});
            skArc(sketch, "E11.27.6", {"start": v(43.78, 2.42) * mm, "mid": v(44.05, 2.73) * mm, "end": v(44.14, 3.13) * mm});
            skArc(sketch, "E11.27.7", {"start": v(38.83, 0.7) * mm, "mid": v(41.43, 1.22) * mm, "end": v(43.78, 2.42) * mm});
            skLineSegment(sketch, "E11.27.8", {"start": v(38.79, 0.7) * mm, "end": v(36.8, 0.7) * mm});
            skArc(sketch, "E11.27.9", {"start": v(36.8, 0.7) * mm, "mid": v(36.22, 0.46) * mm, "end": v(35.98, -0.12) * mm});
            skArc(sketch, "E11.28.0", {"start": v(34.91, 11.66) * mm, "mid": v(34.28, 11.7) * mm, "end": v(33.86, 12.16) * mm});
            skLineSegment(sketch, "E11.28.1", {"start": v(36.78, 12.33) * mm, "end": v(34.91, 11.66) * mm});
            skArc(sketch, "E11.28.2", {"start": v(36.82, 12.34) * mm, "mid": v(39.44, 12.73) * mm, "end": v(42.07, 12.39) * mm});
            skArc(sketch, "E11.28.3", {"start": v(42.07, 12.39) * mm, "mid": v(42.42, 12.18) * mm, "end": v(42.63, 11.83) * mm});
            skLineSegment(sketch, "E11.28.4", {"start": v(42.63, 11.83) * mm, "end": v(42.8, 11.3) * mm});
            skLineSegment(sketch, "E11.28.5", {"start": v(42.92, 10.75) * mm, "end": v(42.8, 11.3) * mm});
            skArc(sketch, "E11.28.6", {"start": v(42.7, 9.99) * mm, "mid": v(42.9, 10.34) * mm, "end": v(42.92, 10.75) * mm});
            skArc(sketch, "E11.28.7", {"start": v(38.12, 7.44) * mm, "mid": v(40.59, 8.4) * mm, "end": v(42.7, 9.99) * mm});
            skLineSegment(sketch, "E11.28.8", {"start": v(38.07, 7.43) * mm, "end": v(36.12, 7.09) * mm});
            skArc(sketch, "E11.28.9", {"start": v(36.12, 7.09) * mm, "mid": v(35.6, 6.75) * mm, "end": v(35.45, 6.13) * mm});
            skArc(sketch, "E11.29.0", {"start": v(32.36, 17.55) * mm, "mid": v(31.73, 17.47) * mm, "end": v(31.23, 17.86) * mm});
            skLineSegment(sketch, "E11.29.1", {"start": v(34.08, 18.53) * mm, "end": v(32.36, 17.55) * mm});
            skArc(sketch, "E11.29.2", {"start": v(34.12, 18.55) * mm, "mid": v(36.63, 19.39) * mm, "end": v(39.28, 19.5) * mm});
            skArc(sketch, "E11.29.3", {"start": v(39.28, 19.5) * mm, "mid": v(39.66, 19.36) * mm, "end": v(39.93, 19.06) * mm});
            skLineSegment(sketch, "E11.29.4", {"start": v(39.93, 19.06) * mm, "end": v(40.19, 18.56) * mm});
            skLineSegment(sketch, "E11.29.5", {"start": v(40.4, 18.04) * mm, "end": v(40.19, 18.56) * mm});
            skArc(sketch, "E11.29.6", {"start": v(40.32, 17.25) * mm, "mid": v(40.46, 17.63) * mm, "end": v(40.4, 18.04) * mm});
            skArc(sketch, "E11.29.7", {"start": v(36.25, 13.95) * mm, "mid": v(38.51, 15.31) * mm, "end": v(40.32, 17.25) * mm});
            skLineSegment(sketch, "E11.29.8", {"start": v(36.2, 13.93) * mm, "end": v(34.34, 13.25) * mm});
            skArc(sketch, "E11.29.9", {"start": v(34.34, 13.25) * mm, "mid": v(33.88, 12.83) * mm, "end": v(33.85, 12.2) * mm});
            skArc(sketch, "E11.30.0", {"start": v(28.82, 22.9) * mm, "mid": v(28.22, 22.72) * mm, "end": v(27.66, 23.01) * mm});
            skLineSegment(sketch, "E11.30.1", {"start": v(30.35, 24.16) * mm, "end": v(28.82, 22.9) * mm});
            skArc(sketch, "E11.30.2", {"start": v(30.38, 24.2) * mm, "mid": v(32.7, 25.45) * mm, "end": v(35.3, 26.03) * mm});
            skArc(sketch, "E11.30.3", {"start": v(35.3, 26.03) * mm, "mid": v(35.7, 25.96) * mm, "end": v(36.02, 25.7) * mm});
            skLineSegment(sketch, "E11.30.4", {"start": v(36.02, 25.7) * mm, "end": v(36.35, 25.25) * mm});
            skLineSegment(sketch, "E11.30.5", {"start": v(36.66, 24.78) * mm, "end": v(36.36, 25.25) * mm});
            skArc(sketch, "E11.30.6", {"start": v(36.7, 23.99) * mm, "mid": v(36.78, 24.4) * mm, "end": v(36.66, 24.78) * mm});
            skArc(sketch, "E11.30.7", {"start": v(33.28, 20.03) * mm, "mid": v(35.27, 21.77) * mm, "end": v(36.7, 23.99) * mm});
            skLineSegment(sketch, "E11.30.8", {"start": v(33.24, 20) * mm, "end": v(31.52, 19.01) * mm});
            skArc(sketch, "E11.30.9", {"start": v(31.52, 19.01) * mm, "mid": v(31.14, 18.51) * mm, "end": v(31.22, 17.89) * mm});
            skArc(sketch, "E11.31.0", {"start": v(24.4, 27.56) * mm, "mid": v(23.84, 27.27) * mm, "end": v(23.24, 27.46) * mm});
            skLineSegment(sketch, "E11.31.1", {"start": v(25.69, 29.07) * mm, "end": v(24.4, 27.56) * mm});
            skArc(sketch, "E11.31.2", {"start": v(25.72, 29.1) * mm, "mid": v(27.8, 30.75) * mm, "end": v(30.24, 31.76) * mm});
            skArc(sketch, "E11.31.3", {"start": v(30.24, 31.76) * mm, "mid": v(30.65, 31.76) * mm, "end": v(31, 31.57) * mm});
            skLineSegment(sketch, "E11.31.4", {"start": v(31, 31.57) * mm, "end": v(31.42, 31.18) * mm});
            skLineSegment(sketch, "E11.31.5", {"start": v(31.8, 30.77) * mm, "end": v(31.42, 31.18) * mm});
            skArc(sketch, "E11.31.6", {"start": v(31.99, 30) * mm, "mid": v(31.99, 30.4) * mm, "end": v(31.8, 30.77) * mm});
            skArc(sketch, "E11.31.7", {"start": v(29.3, 25.5) * mm, "mid": v(30.95, 27.56) * mm, "end": v(31.99, 30) * mm});
            skLineSegment(sketch, "E11.31.8", {"start": v(29.26, 25.47) * mm, "end": v(27.74, 24.2) * mm});
            skArc(sketch, "E11.31.9", {"start": v(27.74, 24.2) * mm, "mid": v(27.45, 23.64) * mm, "end": v(27.64, 23.04) * mm});
            skArc(sketch, "E11.32.0", {"start": v(19.25, 31.38) * mm, "mid": v(18.75, 31) * mm, "end": v(18.12, 31.08) * mm});
            skLineSegment(sketch, "E11.32.1", {"start": v(20.25, 33.09) * mm, "end": v(19.25, 31.38) * mm});
            skArc(sketch, "E11.32.2", {"start": v(20.28, 33.12) * mm, "mid": v(22.03, 35.1) * mm, "end": v(24.26, 36.53) * mm});
            skArc(sketch, "E11.32.3", {"start": v(24.26, 36.53) * mm, "mid": v(24.67, 36.6) * mm, "end": v(25.05, 36.47) * mm});
            skLineSegment(sketch, "E11.32.4", {"start": v(25.05, 36.47) * mm, "end": v(25.52, 36.17) * mm});
            skLineSegment(sketch, "E11.32.5", {"start": v(25.97, 35.82) * mm, "end": v(25.53, 36.16) * mm});
            skArc(sketch, "E11.32.6", {"start": v(26.29, 35.1) * mm, "mid": v(26.22, 35.5) * mm, "end": v(25.97, 35.82) * mm});
            skArc(sketch, "E11.32.7", {"start": v(24.42, 30.2) * mm, "mid": v(25.7, 32.52) * mm, "end": v(26.29, 35.1) * mm});
            skLineSegment(sketch, "E11.32.8", {"start": v(24.4, 30.17) * mm, "end": v(23.12, 28.65) * mm});
            skArc(sketch, "E11.32.9", {"start": v(23.12, 28.65) * mm, "mid": v(22.93, 28.05) * mm, "end": v(23.22, 27.49) * mm});
            skArc(sketch, "E11.33.0", {"start": v(13.5, 34.24) * mm, "mid": v(13.08, 33.78) * mm, "end": v(12.45, 33.76) * mm});
            skLineSegment(sketch, "E11.33.1", {"start": v(14.2, 36.1) * mm, "end": v(13.5, 34.24) * mm});
            skArc(sketch, "E11.33.2", {"start": v(14.22, 36.14) * mm, "mid": v(15.6, 38.4) * mm, "end": v(17.55, 40.19) * mm});
            skArc(sketch, "E11.33.3", {"start": v(17.55, 40.19) * mm, "mid": v(17.94, 40.33) * mm, "end": v(18.34, 40.27) * mm});
            skLineSegment(sketch, "E11.33.4", {"start": v(18.34, 40.27) * mm, "end": v(18.86, 40.05) * mm});
            skLineSegment(sketch, "E11.33.5", {"start": v(19.35, 39.79) * mm, "end": v(18.86, 40.05) * mm});
            skArc(sketch, "E11.33.6", {"start": v(19.8, 39.13) * mm, "mid": v(19.66, 39.52) * mm, "end": v(19.35, 39.79) * mm});
            skArc(sketch, "E11.33.7", {"start": v(18.8, 33.98) * mm, "mid": v(19.66, 36.49) * mm, "end": v(19.8, 39.13) * mm});
            skLineSegment(sketch, "E11.33.8", {"start": v(18.78, 33.94) * mm, "end": v(17.8, 32.23) * mm});
            skArc(sketch, "E11.33.9", {"start": v(17.8, 32.23) * mm, "mid": v(17.7, 31.6) * mm, "end": v(18.1, 31.1) * mm});
            skArc(sketch, "E11.34.0", {"start": v(7.36, 36.07) * mm, "mid": v(7.01, 35.54) * mm, "end": v(6.4, 35.4) * mm});
            skLineSegment(sketch, "E11.34.1", {"start": v(7.71, 38.02) * mm, "end": v(7.36, 36.07) * mm});
            skArc(sketch, "E11.34.2", {"start": v(7.72, 38.06) * mm, "mid": v(8.7, 40.52) * mm, "end": v(10.3, 42.62) * mm});
            skArc(sketch, "E11.34.3", {"start": v(10.3, 42.62) * mm, "mid": v(10.66, 42.83) * mm, "end": v(11.07, 42.84) * mm});
            skLineSegment(sketch, "E11.34.4", {"start": v(11.07, 42.84) * mm, "end": v(11.62, 42.71) * mm});
            skLineSegment(sketch, "E11.34.5", {"start": v(12.15, 42.54) * mm, "end": v(11.62, 42.71) * mm});
            skArc(sketch, "E11.34.6", {"start": v(12.7, 41.97) * mm, "mid": v(12.5, 42.33) * mm, "end": v(12.15, 42.54) * mm});
            skArc(sketch, "E11.34.7", {"start": v(12.62, 36.73) * mm, "mid": v(13.03, 39.35) * mm, "end": v(12.7, 41.97) * mm});
            skLineSegment(sketch, "E11.34.8", {"start": v(12.6, 36.69) * mm, "end": v(11.92, 34.83) * mm});
            skArc(sketch, "E11.34.9", {"start": v(11.92, 34.83) * mm, "mid": v(11.95, 34.2) * mm, "end": v(12.42, 33.77) * mm});
            skArc(sketch, "E11.35.0", {"start": v(0.98, 36.8) * mm, "mid": v(0.74, 36.22) * mm, "end": v(0.15, 35.98) * mm});
            skLineSegment(sketch, "E11.35.1", {"start": v(1, 38.78) * mm, "end": v(0.98, 36.8) * mm});
            skArc(sketch, "E11.35.2", {"start": v(1, 38.82) * mm, "mid": v(1.53, 41.42) * mm, "end": v(2.75, 43.77) * mm});
            skArc(sketch, "E11.35.3", {"start": v(2.75, 43.77) * mm, "mid": v(3.06, 44.03) * mm, "end": v(3.46, 44.11) * mm});
            skLineSegment(sketch, "E11.35.4", {"start": v(3.46, 44.11) * mm, "end": v(4.02, 44.08) * mm});
            skLineSegment(sketch, "E11.35.5", {"start": v(4.58, 44) * mm, "end": v(4.02, 44.08) * mm});
            skArc(sketch, "E11.35.6", {"start": v(5.22, 43.54) * mm, "mid": v(4.96, 43.86) * mm, "end": v(4.58, 44) * mm});
            skArc(sketch, "E11.35.7", {"start": v(6.05, 38.36) * mm, "mid": v(6, 41) * mm, "end": v(5.22, 43.54) * mm});
            skLineSegment(sketch, "E11.35.8", {"start": v(6.04, 38.32) * mm, "end": v(5.7, 36.37) * mm});
            skArc(sketch, "E11.35.9", {"start": v(5.7, 36.37) * mm, "mid": v(5.83, 35.75) * mm, "end": v(6.36, 35.41) * mm});
            skPoint(sketch, "E11.center", {"position": v(0, 0) * mm});
            skLineSegment(sketch, "E12", {"start": v(6.4, 35.4) * mm, "end": v(6.36, 35.41) * mm});
            skLineSegment(sketch, "E13", {"start": v(0.15, 35.98) * mm, "end": v(0.12, 35.98) * mm});
            skLineSegment(sketch, "E14", {"start": v(-6.1, 35.46) * mm, "end": v(-6.13, 35.45) * mm});
            skLineSegment(sketch, "E15", {"start": v(-12.16, 33.86) * mm, "end": v(-12.2, 33.85) * mm});
            skLineSegment(sketch, "E16", {"start": v(-17.86, 31.23) * mm, "end": v(-17.89, 31.22) * mm});
            skLineSegment(sketch, "E17", {"start": v(-23.01, 27.66) * mm, "end": v(-23.04, 27.64) * mm});
            skLineSegment(sketch, "E18", {"start": v(-27.46, 23.24) * mm, "end": v(-27.49, 23.22) * mm});
            skLineSegment(sketch, "E19", {"start": v(-31.08, 18.12) * mm, "end": v(-31.1, 18.1) * mm});
            skLineSegment(sketch, "E20", {"start": v(-33.76, 12.45) * mm, "end": v(-33.77, 12.42) * mm});
            skLineSegment(sketch, "E21", {"start": v(-35.4, 6.4) * mm, "end": v(-35.41, 6.36) * mm});
            skLineSegment(sketch, "E22", {"start": v(-35.98, 0.15) * mm, "end": v(-35.98, 0.12) * mm});
            skLineSegment(sketch, "E23", {"start": v(-35.46, -6.1) * mm, "end": v(-35.45, -6.13) * mm});
            skLineSegment(sketch, "E24", {"start": v(-33.86, -12.16) * mm, "end": v(-33.85, -12.2) * mm});
            skLineSegment(sketch, "E25", {"start": v(-31.22, -17.89) * mm, "end": v(-31.23, -17.86) * mm});
            skLineSegment(sketch, "E26", {"start": v(-27.64, -23.04) * mm, "end": v(-27.66, -23.01) * mm});
            skLineSegment(sketch, "E27", {"start": v(-23.22, -27.49) * mm, "end": v(-23.24, -27.46) * mm});
            skLineSegment(sketch, "E28", {"start": v(-18.1, -31.1) * mm, "end": v(-18.12, -31.08) * mm});
            skLineSegment(sketch, "E29", {"start": v(-12.42, -33.77) * mm, "end": v(-12.45, -33.76) * mm});
            skLineSegment(sketch, "E30", {"start": v(-6.36, -35.41) * mm, "end": v(-6.4, -35.4) * mm});
            skLineSegment(sketch, "E31", {"start": v(-0.12, -35.98) * mm, "end": v(-0.15, -35.98) * mm});
            skLineSegment(sketch, "E32", {"start": v(6.13, -35.45) * mm, "end": v(6.1, -35.46) * mm});
            skLineSegment(sketch, "E33", {"start": v(12.2, -33.85) * mm, "end": v(12.16, -33.86) * mm});
            skLineSegment(sketch, "E34", {"start": v(17.89, -31.22) * mm, "end": v(17.86, -31.23) * mm});
            skLineSegment(sketch, "E35", {"start": v(23.04, -27.64) * mm, "end": v(23.01, -27.66) * mm});
            skLineSegment(sketch, "E36", {"start": v(27.49, -23.22) * mm, "end": v(27.46, -23.24) * mm});
            skLineSegment(sketch, "E37", {"start": v(31.1, -18.1) * mm, "end": v(31.08, -18.12) * mm});
            skLineSegment(sketch, "E38", {"start": v(33.77, -12.42) * mm, "end": v(33.76, -12.45) * mm});
            skLineSegment(sketch, "E39", {"start": v(35.41, -6.36) * mm, "end": v(35.4, -6.4) * mm});
            skLineSegment(sketch, "E40", {"start": v(35.98, -0.12) * mm, "end": v(35.98, -0.15) * mm});
            skLineSegment(sketch, "E41", {"start": v(35.45, 6.13) * mm, "end": v(35.46, 6.1) * mm});
            skLineSegment(sketch, "E42", {"start": v(33.86, 12.16) * mm, "end": v(33.85, 12.2) * mm});
            skLineSegment(sketch, "E43", {"start": v(31.23, 17.86) * mm, "end": v(31.22, 17.89) * mm});
            skLineSegment(sketch, "E44", {"start": v(27.66, 23.01) * mm, "end": v(27.64, 23.04) * mm});
            skLineSegment(sketch, "E45", {"start": v(23.24, 27.46) * mm, "end": v(23.22, 27.49) * mm});
            skLineSegment(sketch, "E46", {"start": v(18.12, 31.08) * mm, "end": v(18.1, 31.1) * mm});
            skLineSegment(sketch, "E47", {"start": v(12.45, 33.76) * mm, "end": v(12.42, 33.77) * mm});
            skLineSegment(sketch, "E48", {"start": v(-3.7, 44.11) * mm, "end": v(-3.7, 44.11) * mm});
            skLineSegment(sketch, "E49", {"start": v(-11.3, 42.8) * mm, "end": v(-11.3, 42.8) * mm});
            skLineSegment(sketch, "E50", {"start": v(-18.56, 40.19) * mm, "end": v(-18.56, 40.19) * mm});
            skLineSegment(sketch, "E51", {"start": v(-25.25, 36.35) * mm, "end": v(-25.25, 36.36) * mm});
            skLineSegment(sketch, "E52", {"start": v(-31.18, 31.42) * mm, "end": v(-31.18, 31.42) * mm});
            skLineSegment(sketch, "E53", {"start": v(-36.17, 25.52) * mm, "end": v(-36.16, 25.53) * mm});
            skLineSegment(sketch, "E54", {"start": v(-40.05, 18.86) * mm, "end": v(-40.05, 18.86) * mm});
            skLineSegment(sketch, "E55", {"start": v(-42.71, 11.62) * mm, "end": v(-42.71, 11.62) * mm});
            skLineSegment(sketch, "E56", {"start": v(-44.08, 4.02) * mm, "end": v(-44.08, 4.02) * mm});
            skLineSegment(sketch, "E57", {"start": v(-44.11, -3.7) * mm, "end": v(-44.11, -3.7) * mm});
            skLineSegment(sketch, "E58", {"start": v(-42.8, -11.3) * mm, "end": v(-42.8, -11.3) * mm});
            skLineSegment(sketch, "E59", {"start": v(-40.19, -18.56) * mm, "end": v(-40.19, -18.56) * mm});
            skLineSegment(sketch, "E60", {"start": v(-36.36, -25.25) * mm, "end": v(-36.35, -25.25) * mm});
            skLineSegment(sketch, "E61", {"start": v(-31.42, -31.18) * mm, "end": v(-31.42, -31.18) * mm});
            skLineSegment(sketch, "E62", {"start": v(-25.53, -36.16) * mm, "end": v(-25.52, -36.17) * mm});
            skLineSegment(sketch, "E63", {"start": v(-18.86, -40.05) * mm, "end": v(-18.86, -40.05) * mm});
            skLineSegment(sketch, "E64", {"start": v(-11.62, -42.71) * mm, "end": v(-11.62, -42.71) * mm});
            skLineSegment(sketch, "E65", {"start": v(-4.02, -44.08) * mm, "end": v(-4.02, -44.08) * mm});
            skLineSegment(sketch, "E66", {"start": v(3.7, -44.11) * mm, "end": v(3.7, -44.11) * mm});
            skLineSegment(sketch, "E67", {"start": v(11.3, -42.8) * mm, "end": v(11.3, -42.8) * mm});
            skLineSegment(sketch, "E68", {"start": v(18.56, -40.19) * mm, "end": v(18.56, -40.19) * mm});
            skLineSegment(sketch, "E69", {"start": v(25.25, -36.36) * mm, "end": v(25.25, -36.35) * mm});
            skLineSegment(sketch, "E70", {"start": v(31.18, -31.42) * mm, "end": v(31.18, -31.42) * mm});
            skLineSegment(sketch, "E71", {"start": v(36.17, -25.52) * mm, "end": v(36.16, -25.53) * mm});
            skLineSegment(sketch, "E72", {"start": v(40.05, -18.86) * mm, "end": v(40.05, -18.86) * mm});
            skLineSegment(sketch, "E73", {"start": v(42.71, -11.62) * mm, "end": v(42.71, -11.62) * mm});
            skLineSegment(sketch, "E74", {"start": v(44.08, -4.02) * mm, "end": v(44.08, -4.02) * mm});
            skLineSegment(sketch, "E75", {"start": v(44.11, 3.7) * mm, "end": v(44.11, 3.7) * mm});
            skLineSegment(sketch, "E76", {"start": v(42.8, 11.3) * mm, "end": v(42.8, 11.3) * mm});
            skLineSegment(sketch, "E77", {"start": v(40.19, 18.56) * mm, "end": v(40.19, 18.56) * mm});
            skLineSegment(sketch, "E78", {"start": v(36.35, 25.25) * mm, "end": v(36.36, 25.25) * mm});
            skLineSegment(sketch, "E79", {"start": v(31.42, 31.18) * mm, "end": v(31.42, 31.18) * mm});
            skLineSegment(sketch, "E80", {"start": v(25.52, 36.17) * mm, "end": v(25.53, 36.16) * mm});
            skLineSegment(sketch, "E81", {"start": v(18.86, 40.05) * mm, "end": v(18.86, 40.05) * mm});
            skLineSegment(sketch, "E82", {"start": v(11.62, 42.71) * mm, "end": v(11.62, 42.71) * mm});
            skLineSegment(sketch, "E83", {"start": v(4.02, 44.08) * mm, "end": v(4.02, 44.08) * mm});
            skLineSegment(sketch, "E84", {"start": v(33.24, 20) * mm, "end": v(33.28, 20.03) * mm});
            skLineSegment(sketch, "E85", {"start": v(30.35, 24.16) * mm, "end": v(30.38, 24.2) * mm});
            skLineSegment(sketch, "E86", {"start": v(29.26, 25.47) * mm, "end": v(29.3, 25.5) * mm});
            skLineSegment(sketch, "E87", {"start": v(25.69, 29.07) * mm, "end": v(25.72, 29.1) * mm});
            skLineSegment(sketch, "E88", {"start": v(24.4, 30.17) * mm, "end": v(24.42, 30.2) * mm});
            skLineSegment(sketch, "E89", {"start": v(20.28, 33.12) * mm, "end": v(20.25, 33.09) * mm});
            skLineSegment(sketch, "E90", {"start": v(18.78, 33.94) * mm, "end": v(18.8, 33.98) * mm});
            skLineSegment(sketch, "E91", {"start": v(14.22, 36.14) * mm, "end": v(14.2, 36.1) * mm});
            skLineSegment(sketch, "E92", {"start": v(12.62, 36.73) * mm, "end": v(12.6, 36.69) * mm});
            skLineSegment(sketch, "E93", {"start": v(7.72, 38.06) * mm, "end": v(7.71, 38.02) * mm});
            skLineSegment(sketch, "E94", {"start": v(6.05, 38.36) * mm, "end": v(6.04, 38.32) * mm});
            skLineSegment(sketch, "E95", {"start": v(1, 38.82) * mm, "end": v(1, 38.78) * mm});
            skLineSegment(sketch, "E96", {"start": v(-5.76, 38.4) * mm, "end": v(-5.75, 38.36) * mm});
            skLineSegment(sketch, "E97", {"start": v(-7.44, 38.12) * mm, "end": v(-7.43, 38.07) * mm});
            skLineSegment(sketch, "E98", {"start": v(-12.34, 36.82) * mm, "end": v(-12.33, 36.78) * mm});
            skLineSegment(sketch, "E99", {"start": v(-13.95, 36.25) * mm, "end": v(-13.93, 36.2) * mm});
            skLineSegment(sketch, "E100", {"start": v(-18.55, 34.12) * mm, "end": v(-18.53, 34.08) * mm});
            skLineSegment(sketch, "E101", {"start": v(-20.03, 33.28) * mm, "end": v(-20, 33.24) * mm});
            skLineSegment(sketch, "E102", {"start": v(-24.2, 30.38) * mm, "end": v(-24.16, 30.35) * mm});
            skLineSegment(sketch, "E103", {"start": v(-25.5, 29.3) * mm, "end": v(-25.47, 29.26) * mm});
            skLineSegment(sketch, "E104", {"start": v(-29.1, 25.72) * mm, "end": v(-29.07, 25.69) * mm});
            skLineSegment(sketch, "E105", {"start": v(-30.2, 24.42) * mm, "end": v(-30.17, 24.4) * mm});
            skLineSegment(sketch, "E106", {"start": v(-33.09, 20.25) * mm, "end": v(-33.12, 20.28) * mm});
            skLineSegment(sketch, "E107", {"start": v(-33.98, 18.8) * mm, "end": v(-33.94, 18.78) * mm});
            skLineSegment(sketch, "E108", {"start": v(-36.14, 14.22) * mm, "end": v(-36.1, 14.2) * mm});
            skLineSegment(sketch, "E109", {"start": v(-36.73, 12.62) * mm, "end": v(-36.69, 12.6) * mm});
            skLineSegment(sketch, "E110", {"start": v(-38.06, 7.72) * mm, "end": v(-38.02, 7.71) * mm});
            skLineSegment(sketch, "E111", {"start": v(-38.36, 6.05) * mm, "end": v(-38.32, 6.04) * mm});
            skLineSegment(sketch, "E112", {"start": v(-38.82, 1) * mm, "end": v(-38.78, 1) * mm});
            skLineSegment(sketch, "E113", {"start": v(-38.83, -0.7) * mm, "end": v(-38.79, -0.7) * mm});
            skLineSegment(sketch, "E114", {"start": v(-38.4, -5.76) * mm, "end": v(-38.36, -5.75) * mm});
            skLineSegment(sketch, "E115", {"start": v(-38.12, -7.44) * mm, "end": v(-38.07, -7.43) * mm});
            skLineSegment(sketch, "E116", {"start": v(-36.82, -12.34) * mm, "end": v(-36.78, -12.33) * mm});
            skLineSegment(sketch, "E117", {"start": v(-36.25, -13.95) * mm, "end": v(-36.2, -13.93) * mm});
            skLineSegment(sketch, "E118", {"start": v(-34.12, -18.55) * mm, "end": v(-34.08, -18.53) * mm});
            skLineSegment(sketch, "E119", {"start": v(-33.28, -20.03) * mm, "end": v(-33.24, -20) * mm});
            skLineSegment(sketch, "E120", {"start": v(-30.35, -24.16) * mm, "end": v(-30.38, -24.2) * mm});
            skLineSegment(sketch, "E121", {"start": v(-29.26, -25.47) * mm, "end": v(-29.3, -25.5) * mm});
            skLineSegment(sketch, "E122", {"start": v(-25.69, -29.07) * mm, "end": v(-25.72, -29.1) * mm});
            skLineSegment(sketch, "E123", {"start": v(-24.42, -30.2) * mm, "end": v(-24.4, -30.17) * mm});
            skLineSegment(sketch, "E124", {"start": v(-20.25, -33.09) * mm, "end": v(-20.28, -33.12) * mm});
            skLineSegment(sketch, "E125", {"start": v(-18.78, -33.94) * mm, "end": v(-18.8, -33.98) * mm});
            skLineSegment(sketch, "E126", {"start": v(-14.22, -36.14) * mm, "end": v(-14.2, -36.1) * mm});
            skLineSegment(sketch, "E127", {"start": v(-12.6, -36.69) * mm, "end": v(-12.62, -36.73) * mm});
            skLineSegment(sketch, "E128", {"start": v(-7.72, -38.06) * mm, "end": v(-7.71, -38.02) * mm});
            skLineSegment(sketch, "E129", {"start": v(-6.05, -38.36) * mm, "end": v(-6.04, -38.32) * mm});
            skLineSegment(sketch, "E130", {"start": v(-1, -38.82) * mm, "end": v(-1, -38.78) * mm});
            skLineSegment(sketch, "E131", {"start": v(0.7, -38.79) * mm, "end": v(0.7, -38.83) * mm});
            skLineSegment(sketch, "E132", {"start": v(5.76, -38.4) * mm, "end": v(5.75, -38.36) * mm});
            skLineSegment(sketch, "E133", {"start": v(7.43, -38.07) * mm, "end": v(7.44, -38.12) * mm});
            skLineSegment(sketch, "E134", {"start": v(12.33, -36.78) * mm, "end": v(12.34, -36.82) * mm});
            skLineSegment(sketch, "E135", {"start": v(13.93, -36.2) * mm, "end": v(13.95, -36.25) * mm});
            skLineSegment(sketch, "E136", {"start": v(18.53, -34.08) * mm, "end": v(18.55, -34.12) * mm});
            skLineSegment(sketch, "E137", {"start": v(20.03, -33.28) * mm, "end": v(20, -33.24) * mm});
            skLineSegment(sketch, "E138", {"start": v(24.16, -30.35) * mm, "end": v(24.2, -30.38) * mm});
            skLineSegment(sketch, "E139", {"start": v(25.47, -29.26) * mm, "end": v(25.5, -29.3) * mm});
            skLineSegment(sketch, "E140", {"start": v(29.07, -25.69) * mm, "end": v(29.1, -25.72) * mm});
            skLineSegment(sketch, "E141", {"start": v(30.17, -24.4) * mm, "end": v(30.2, -24.42) * mm});
            skLineSegment(sketch, "E142", {"start": v(33.09, -20.25) * mm, "end": v(33.12, -20.28) * mm});
            skLineSegment(sketch, "E143", {"start": v(33.94, -18.78) * mm, "end": v(33.98, -18.8) * mm});
            skLineSegment(sketch, "E144", {"start": v(36.1, -14.2) * mm, "end": v(36.14, -14.22) * mm});
            skLineSegment(sketch, "E145", {"start": v(36.69, -12.6) * mm, "end": v(36.73, -12.62) * mm});
            skLineSegment(sketch, "E146", {"start": v(38.02, -7.71) * mm, "end": v(38.06, -7.72) * mm});
            skLineSegment(sketch, "E147", {"start": v(38.32, -6.04) * mm, "end": v(38.36, -6.05) * mm});
            skLineSegment(sketch, "E148", {"start": v(38.78, -1) * mm, "end": v(38.82, -1) * mm});
            skLineSegment(sketch, "E149", {"start": v(38.79, 0.7) * mm, "end": v(38.83, 0.7) * mm});
            skLineSegment(sketch, "E150", {"start": v(38.07, 7.43) * mm, "end": v(38.12, 7.44) * mm});
            skLineSegment(sketch, "E151", {"start": v(38.36, 5.75) * mm, "end": v(38.4, 5.76) * mm});
            skLineSegment(sketch, "E152", {"start": v(36.2, 13.93) * mm, "end": v(36.25, 13.95) * mm});
            skLineSegment(sketch, "E153", {"start": v(36.78, 12.33) * mm, "end": v(36.82, 12.34) * mm});
            skLineSegment(sketch, "E154", {"start": v(34.08, 18.53) * mm, "end": v(34.12, 18.55) * mm});
            skSolve(sketch);
        }
        {
            var Q0;
            Q0=makeQuery(id+"F0.imprint","IMPRINT",FACE,{"disambiguationData":[TD([[makeQuery(id+"F0.imprint","IMPRINT",EDGE,{"derivedFrom":sQuery(id+"F0.wireOp",EDGE,"E0.trimOffspring")}),1.0]])]});
            extrude(context, id + "F1", {"entities" : qUnion([Q0]), "depth" : 12.7 * mm});
        }
        {
            var Q0;
            Q0=makeQuery(id+"F1.opExtrude","CAP_FACE",FACE,{"disambiguationData":[OSD([sQuery(id+"F0.wireOp",EDGE,"E0.trimOffspring"),sQuery(id+"F0.wireOp",EDGE,"E1"),sQuery(id+"F0.wireOp",EDGE,"E2"),sQuery(id+"F0.wireOp",EDGE,"E3.filletArc"),sQuery(id+"F0.wireOp",EDGE,"E4.filletArc"),sQuery(id+"F0.wireOp",EDGE,"E5.filletArc"),sQuery(id+"F0.wireOp",EDGE,"E6.MirrorCS"),sQuery(id+"F0.wireOp",EDGE,"E7.MirrorCS"),sQuery(id+"F0.wireOp",EDGE,"E8.MirrorCS"),sQuery(id+"F0.wireOp",EDGE,"E9.MirrorCS"),sQuery(id+"F0.wireOp",EDGE,"E10.MirrorCS"),sQuery(id+"F0.wireOp",EDGE,"E11.1.0"),sQuery(id+"F0.wireOp",EDGE,"E11.1.1"),sQuery(id+"F0.wireOp",EDGE,"E11.1.2"),sQuery(id+"F0.wireOp",EDGE,"E11.1.3"),sQuery(id+"F0.wireOp",EDGE,"E11.1.4"),sQuery(id+"F0.wireOp",EDGE,"E11.1.5"),sQuery(id+"F0.wireOp",EDGE,"E11.1.6"),sQuery(id+"F0.wireOp",EDGE,"E11.1.7"),sQuery(id+"F0.wireOp",EDGE,"E11.1.8"),sQuery(id+"F0.wireOp",EDGE,"E11.1.9"),sQuery(id+"F0.wireOp",EDGE,"E11.2.0"),sQuery(id+"F0.wireOp",EDGE,"E11.2.1"),sQuery(id+"F0.wireOp",EDGE,"E11.2.2"),sQuery(id+"F0.wireOp",EDGE,"E11.2.3"),sQuery(id+"F0.wireOp",EDGE,"E11.2.4"),sQuery(id+"F0.wireOp",EDGE,"E11.2.5"),sQuery(id+"F0.wireOp",EDGE,"E11.2.6"),sQuery(id+"F0.wireOp",EDGE,"E11.2.7"),sQuery(id+"F0.wireOp",EDGE,"E11.2.8"),sQuery(id+"F0.wireOp",EDGE,"E11.2.9"),sQuery(id+"F0.wireOp",EDGE,"E11.3.0"),sQuery(id+"F0.wireOp",EDGE,"E11.3.1"),sQuery(id+"F0.wireOp",EDGE,"E11.3.2"),sQuery(id+"F0.wireOp",EDGE,"E11.3.3"),sQuery(id+"F0.wireOp",EDGE,"E11.3.4"),sQuery(id+"F0.wireOp",EDGE,"E11.3.5"),sQuery(id+"F0.wireOp",EDGE,"E11.3.6"),sQuery(id+"F0.wireOp",EDGE,"E11.3.7"),sQuery(id+"F0.wireOp",EDGE,"E11.3.8"),sQuery(id+"F0.wireOp",EDGE,"E11.3.9"),sQuery(id+"F0.wireOp",EDGE,"E11.4.0"),sQuery(id+"F0.wireOp",EDGE,"E11.4.1"),sQuery(id+"F0.wireOp",EDGE,"E11.4.2"),sQuery(id+"F0.wireOp",EDGE,"E11.4.3"),sQuery(id+"F0.wireOp",EDGE,"E11.4.4"),sQuery(id+"F0.wireOp",EDGE,"E11.4.5"),sQuery(id+"F0.wireOp",EDGE,"E11.4.6"),sQuery(id+"F0.wireOp",EDGE,"E11.4.7"),sQuery(id+"F0.wireOp",EDGE,"E11.4.8"),sQuery(id+"F0.wireOp",EDGE,"E11.4.9"),sQuery(id+"F0.wireOp",EDGE,"E11.5.0"),sQuery(id+"F0.wireOp",EDGE,"E11.5.1"),sQuery(id+"F0.wireOp",EDGE,"E11.5.2"),sQuery(id+"F0.wireOp",EDGE,"E11.5.3"),sQuery(id+"F0.wireOp",EDGE,"E11.5.4"),sQuery(id+"F0.wireOp",EDGE,"E11.5.5"),sQuery(id+"F0.wireOp",EDGE,"E11.5.6"),sQuery(id+"F0.wireOp",EDGE,"E11.5.7"),sQuery(id+"F0.wireOp",EDGE,"E11.5.8"),sQuery(id+"F0.wireOp",EDGE,"E11.5.9"),sQuery(id+"F0.wireOp",EDGE,"E11.6.0"),sQuery(id+"F0.wireOp",EDGE,"E11.6.1"),sQuery(id+"F0.wireOp",EDGE,"E11.6.2"),sQuery(id+"F0.wireOp",EDGE,"E11.6.3"),sQuery(id+"F0.wireOp",EDGE,"E11.6.4"),sQuery(id+"F0.wireOp",EDGE,"E11.6.5"),sQuery(id+"F0.wireOp",EDGE,"E11.6.6"),sQuery(id+"F0.wireOp",EDGE,"E11.6.7"),sQuery(id+"F0.wireOp",EDGE,"E11.6.8"),sQuery(id+"F0.wireOp",EDGE,"E11.6.9"),sQuery(id+"F0.wireOp",EDGE,"E11.7.0"),sQuery(id+"F0.wireOp",EDGE,"E11.7.1"),sQuery(id+"F0.wireOp",EDGE,"E11.7.2"),sQuery(id+"F0.wireOp",EDGE,"E11.7.3"),sQuery(id+"F0.wireOp",EDGE,"E11.7.4"),sQuery(id+"F0.wireOp",EDGE,"E11.7.5"),sQuery(id+"F0.wireOp",EDGE,"E11.7.6"),sQuery(id+"F0.wireOp",EDGE,"E11.7.7"),sQuery(id+"F0.wireOp",EDGE,"E11.7.8"),sQuery(id+"F0.wireOp",EDGE,"E11.7.9"),sQuery(id+"F0.wireOp",EDGE,"E11.8.0"),sQuery(id+"F0.wireOp",EDGE,"E11.8.1"),sQuery(id+"F0.wireOp",EDGE,"E11.8.2"),sQuery(id+"F0.wireOp",EDGE,"E11.8.3"),sQuery(id+"F0.wireOp",EDGE,"E11.8.4"),sQuery(id+"F0.wireOp",EDGE,"E11.8.5"),sQuery(id+"F0.wireOp",EDGE,"E11.8.6"),sQuery(id+"F0.wireOp",EDGE,"E11.8.7"),sQuery(id+"F0.wireOp",EDGE,"E11.8.8"),sQuery(id+"F0.wireOp",EDGE,"E11.8.9"),sQuery(id+"F0.wireOp",EDGE,"E11.9.0"),sQuery(id+"F0.wireOp",EDGE,"E11.9.1"),sQuery(id+"F0.wireOp",EDGE,"E11.9.2"),sQuery(id+"F0.wireOp",EDGE,"E11.9.3"),sQuery(id+"F0.wireOp",EDGE,"E11.9.4"),sQuery(id+"F0.wireOp",EDGE,"E11.9.5"),sQuery(id+"F0.wireOp",EDGE,"E11.9.6"),sQuery(id+"F0.wireOp",EDGE,"E11.9.7"),sQuery(id+"F0.wireOp",EDGE,"E11.9.8"),sQuery(id+"F0.wireOp",EDGE,"E11.9.9"),sQuery(id+"F0.wireOp",EDGE,"E11.10.0"),sQuery(id+"F0.wireOp",EDGE,"E11.10.1"),sQuery(id+"F0.wireOp",EDGE,"E11.10.2"),sQuery(id+"F0.wireOp",EDGE,"E11.10.3"),sQuery(id+"F0.wireOp",EDGE,"E11.10.4"),sQuery(id+"F0.wireOp",EDGE,"E11.10.5"),sQuery(id+"F0.wireOp",EDGE,"E11.10.6"),sQuery(id+"F0.wireOp",EDGE,"E11.10.7"),sQuery(id+"F0.wireOp",EDGE,"E11.10.8"),sQuery(id+"F0.wireOp",EDGE,"E11.10.9"),sQuery(id+"F0.wireOp",EDGE,"E11.11.0"),sQuery(id+"F0.wireOp",EDGE,"E11.11.1"),sQuery(id+"F0.wireOp",EDGE,"E11.11.2"),sQuery(id+"F0.wireOp",EDGE,"E11.11.3"),sQuery(id+"F0.wireOp",EDGE,"E11.11.4"),sQuery(id+"F0.wireOp",EDGE,"E11.11.5"),sQuery(id+"F0.wireOp",EDGE,"E11.11.6"),sQuery(id+"F0.wireOp",EDGE,"E11.11.7"),sQuery(id+"F0.wireOp",EDGE,"E11.11.8"),sQuery(id+"F0.wireOp",EDGE,"E11.11.9"),sQuery(id+"F0.wireOp",EDGE,"E11.12.0"),sQuery(id+"F0.wireOp",EDGE,"E11.12.1"),sQuery(id+"F0.wireOp",EDGE,"E11.12.2"),sQuery(id+"F0.wireOp",EDGE,"E11.12.3"),sQuery(id+"F0.wireOp",EDGE,"E11.12.4"),sQuery(id+"F0.wireOp",EDGE,"E11.12.5"),sQuery(id+"F0.wireOp",EDGE,"E11.12.6"),sQuery(id+"F0.wireOp",EDGE,"E11.12.7"),sQuery(id+"F0.wireOp",EDGE,"E11.12.8"),sQuery(id+"F0.wireOp",EDGE,"E11.12.9"),sQuery(id+"F0.wireOp",EDGE,"E11.13.0"),sQuery(id+"F0.wireOp",EDGE,"E11.13.1"),sQuery(id+"F0.wireOp",EDGE,"E11.13.2"),sQuery(id+"F0.wireOp",EDGE,"E11.13.3"),sQuery(id+"F0.wireOp",EDGE,"E11.13.4"),sQuery(id+"F0.wireOp",EDGE,"E11.13.5"),sQuery(id+"F0.wireOp",EDGE,"E11.13.6"),sQuery(id+"F0.wireOp",EDGE,"E11.13.7"),sQuery(id+"F0.wireOp",EDGE,"E11.13.8"),sQuery(id+"F0.wireOp",EDGE,"E11.13.9"),sQuery(id+"F0.wireOp",EDGE,"E11.14.0"),sQuery(id+"F0.wireOp",EDGE,"E11.14.1"),sQuery(id+"F0.wireOp",EDGE,"E11.14.2"),sQuery(id+"F0.wireOp",EDGE,"E11.14.3"),sQuery(id+"F0.wireOp",EDGE,"E11.14.4"),sQuery(id+"F0.wireOp",EDGE,"E11.14.5"),sQuery(id+"F0.wireOp",EDGE,"E11.14.6"),sQuery(id+"F0.wireOp",EDGE,"E11.14.7"),sQuery(id+"F0.wireOp",EDGE,"E11.14.8"),sQuery(id+"F0.wireOp",EDGE,"E11.14.9"),sQuery(id+"F0.wireOp",EDGE,"E11.15.0"),sQuery(id+"F0.wireOp",EDGE,"E11.15.1"),sQuery(id+"F0.wireOp",EDGE,"E11.15.2"),sQuery(id+"F0.wireOp",EDGE,"E11.15.3"),sQuery(id+"F0.wireOp",EDGE,"E11.15.4"),sQuery(id+"F0.wireOp",EDGE,"E11.15.5"),sQuery(id+"F0.wireOp",EDGE,"E11.15.6"),sQuery(id+"F0.wireOp",EDGE,"E11.15.7"),sQuery(id+"F0.wireOp",EDGE,"E11.15.8"),sQuery(id+"F0.wireOp",EDGE,"E11.15.9"),sQuery(id+"F0.wireOp",EDGE,"E11.16.0"),sQuery(id+"F0.wireOp",EDGE,"E11.16.1"),sQuery(id+"F0.wireOp",EDGE,"E11.16.2"),sQuery(id+"F0.wireOp",EDGE,"E11.16.3"),sQuery(id+"F0.wireOp",EDGE,"E11.16.4"),sQuery(id+"F0.wireOp",EDGE,"E11.16.5"),sQuery(id+"F0.wireOp",EDGE,"E11.16.6"),sQuery(id+"F0.wireOp",EDGE,"E11.16.7"),sQuery(id+"F0.wireOp",EDGE,"E11.16.8"),sQuery(id+"F0.wireOp",EDGE,"E11.16.9"),sQuery(id+"F0.wireOp",EDGE,"E11.17.0"),sQuery(id+"F0.wireOp",EDGE,"E11.17.1"),sQuery(id+"F0.wireOp",EDGE,"E11.17.2"),sQuery(id+"F0.wireOp",EDGE,"E11.17.3"),sQuery(id+"F0.wireOp",EDGE,"E11.17.4"),sQuery(id+"F0.wireOp",EDGE,"E11.17.5"),sQuery(id+"F0.wireOp",EDGE,"E11.17.6"),sQuery(id+"F0.wireOp",EDGE,"E11.17.7"),sQuery(id+"F0.wireOp",EDGE,"E11.17.8"),sQuery(id+"F0.wireOp",EDGE,"E11.17.9"),sQuery(id+"F0.wireOp",EDGE,"E11.18.0"),sQuery(id+"F0.wireOp",EDGE,"E11.18.1"),sQuery(id+"F0.wireOp",EDGE,"E11.18.2"),sQuery(id+"F0.wireOp",EDGE,"E11.18.3"),sQuery(id+"F0.wireOp",EDGE,"E11.18.4"),sQuery(id+"F0.wireOp",EDGE,"E11.18.5"),sQuery(id+"F0.wireOp",EDGE,"E11.18.6"),sQuery(id+"F0.wireOp",EDGE,"E11.18.7"),sQuery(id+"F0.wireOp",EDGE,"E11.18.8"),sQuery(id+"F0.wireOp",EDGE,"E11.18.9"),sQuery(id+"F0.wireOp",EDGE,"E11.19.0"),sQuery(id+"F0.wireOp",EDGE,"E11.19.1"),sQuery(id+"F0.wireOp",EDGE,"E11.19.2"),sQuery(id+"F0.wireOp",EDGE,"E11.19.3"),sQuery(id+"F0.wireOp",EDGE,"E11.19.4"),sQuery(id+"F0.wireOp",EDGE,"E11.19.5"),sQuery(id+"F0.wireOp",EDGE,"E11.19.6"),sQuery(id+"F0.wireOp",EDGE,"E11.19.7"),sQuery(id+"F0.wireOp",EDGE,"E11.19.8"),sQuery(id+"F0.wireOp",EDGE,"E11.19.9"),sQuery(id+"F0.wireOp",EDGE,"E11.20.0"),sQuery(id+"F0.wireOp",EDGE,"E11.20.1"),sQuery(id+"F0.wireOp",EDGE,"E11.20.2"),sQuery(id+"F0.wireOp",EDGE,"E11.20.3"),sQuery(id+"F0.wireOp",EDGE,"E11.20.4"),sQuery(id+"F0.wireOp",EDGE,"E11.20.5"),sQuery(id+"F0.wireOp",EDGE,"E11.20.6"),sQuery(id+"F0.wireOp",EDGE,"E11.20.7"),sQuery(id+"F0.wireOp",EDGE,"E11.20.8"),sQuery(id+"F0.wireOp",EDGE,"E11.20.9"),sQuery(id+"F0.wireOp",EDGE,"E11.21.0"),sQuery(id+"F0.wireOp",EDGE,"E11.21.1"),sQuery(id+"F0.wireOp",EDGE,"E11.21.2"),sQuery(id+"F0.wireOp",EDGE,"E11.21.3"),sQuery(id+"F0.wireOp",EDGE,"E11.21.4"),sQuery(id+"F0.wireOp",EDGE,"E11.21.5"),sQuery(id+"F0.wireOp",EDGE,"E11.21.6"),sQuery(id+"F0.wireOp",EDGE,"E11.21.7"),sQuery(id+"F0.wireOp",EDGE,"E11.21.8"),sQuery(id+"F0.wireOp",EDGE,"E11.21.9"),sQuery(id+"F0.wireOp",EDGE,"E11.22.0"),sQuery(id+"F0.wireOp",EDGE,"E11.22.1"),sQuery(id+"F0.wireOp",EDGE,"E11.22.2"),sQuery(id+"F0.wireOp",EDGE,"E11.22.3"),sQuery(id+"F0.wireOp",EDGE,"E11.22.4"),sQuery(id+"F0.wireOp",EDGE,"E11.22.5"),sQuery(id+"F0.wireOp",EDGE,"E11.22.6"),sQuery(id+"F0.wireOp",EDGE,"E11.22.7"),sQuery(id+"F0.wireOp",EDGE,"E11.22.8"),sQuery(id+"F0.wireOp",EDGE,"E11.22.9"),sQuery(id+"F0.wireOp",EDGE,"E11.23.0"),sQuery(id+"F0.wireOp",EDGE,"E11.23.1"),sQuery(id+"F0.wireOp",EDGE,"E11.23.2"),sQuery(id+"F0.wireOp",EDGE,"E11.23.3"),sQuery(id+"F0.wireOp",EDGE,"E11.23.4"),sQuery(id+"F0.wireOp",EDGE,"E11.23.5"),sQuery(id+"F0.wireOp",EDGE,"E11.23.6"),sQuery(id+"F0.wireOp",EDGE,"E11.23.7"),sQuery(id+"F0.wireOp",EDGE,"E11.23.8"),sQuery(id+"F0.wireOp",EDGE,"E11.23.9"),sQuery(id+"F0.wireOp",EDGE,"E11.24.0"),sQuery(id+"F0.wireOp",EDGE,"E11.24.1"),sQuery(id+"F0.wireOp",EDGE,"E11.24.2"),sQuery(id+"F0.wireOp",EDGE,"E11.24.3"),sQuery(id+"F0.wireOp",EDGE,"E11.24.4"),sQuery(id+"F0.wireOp",EDGE,"E11.24.5"),sQuery(id+"F0.wireOp",EDGE,"E11.24.6"),sQuery(id+"F0.wireOp",EDGE,"E11.24.7"),sQuery(id+"F0.wireOp",EDGE,"E11.24.8"),sQuery(id+"F0.wireOp",EDGE,"E11.24.9"),sQuery(id+"F0.wireOp",EDGE,"E11.25.0"),sQuery(id+"F0.wireOp",EDGE,"E11.25.1"),sQuery(id+"F0.wireOp",EDGE,"E11.25.2"),sQuery(id+"F0.wireOp",EDGE,"E11.25.3"),sQuery(id+"F0.wireOp",EDGE,"E11.25.4"),sQuery(id+"F0.wireOp",EDGE,"E11.25.5"),sQuery(id+"F0.wireOp",EDGE,"E11.25.6"),sQuery(id+"F0.wireOp",EDGE,"E11.25.7"),sQuery(id+"F0.wireOp",EDGE,"E11.25.8"),sQuery(id+"F0.wireOp",EDGE,"E11.25.9"),sQuery(id+"F0.wireOp",EDGE,"E11.26.0"),sQuery(id+"F0.wireOp",EDGE,"E11.26.1"),sQuery(id+"F0.wireOp",EDGE,"E11.26.2"),sQuery(id+"F0.wireOp",EDGE,"E11.26.3"),sQuery(id+"F0.wireOp",EDGE,"E11.26.4"),sQuery(id+"F0.wireOp",EDGE,"E11.26.5"),sQuery(id+"F0.wireOp",EDGE,"E11.26.6"),sQuery(id+"F0.wireOp",EDGE,"E11.26.7"),sQuery(id+"F0.wireOp",EDGE,"E11.26.8"),sQuery(id+"F0.wireOp",EDGE,"E11.26.9"),sQuery(id+"F0.wireOp",EDGE,"E11.27.0"),sQuery(id+"F0.wireOp",EDGE,"E11.27.1"),sQuery(id+"F0.wireOp",EDGE,"E11.27.2"),sQuery(id+"F0.wireOp",EDGE,"E11.27.3"),sQuery(id+"F0.wireOp",EDGE,"E11.27.4"),sQuery(id+"F0.wireOp",EDGE,"E11.27.5"),sQuery(id+"F0.wireOp",EDGE,"E11.27.6"),sQuery(id+"F0.wireOp",EDGE,"E11.27.7"),sQuery(id+"F0.wireOp",EDGE,"E11.27.8"),sQuery(id+"F0.wireOp",EDGE,"E11.27.9"),sQuery(id+"F0.wireOp",EDGE,"E11.28.0"),sQuery(id+"F0.wireOp",EDGE,"E11.28.1"),sQuery(id+"F0.wireOp",EDGE,"E11.28.2"),sQuery(id+"F0.wireOp",EDGE,"E11.28.3"),sQuery(id+"F0.wireOp",EDGE,"E11.28.4"),sQuery(id+"F0.wireOp",EDGE,"E11.28.5"),sQuery(id+"F0.wireOp",EDGE,"E11.28.6"),sQuery(id+"F0.wireOp",EDGE,"E11.28.7"),sQuery(id+"F0.wireOp",EDGE,"E11.28.8"),sQuery(id+"F0.wireOp",EDGE,"E11.28.9"),sQuery(id+"F0.wireOp",EDGE,"E11.29.0"),sQuery(id+"F0.wireOp",EDGE,"E11.29.1"),sQuery(id+"F0.wireOp",EDGE,"E11.29.2"),sQuery(id+"F0.wireOp",EDGE,"E11.29.3"),sQuery(id+"F0.wireOp",EDGE,"E11.29.4"),sQuery(id+"F0.wireOp",EDGE,"E11.29.5"),sQuery(id+"F0.wireOp",EDGE,"E11.29.6"),sQuery(id+"F0.wireOp",EDGE,"E11.29.7"),sQuery(id+"F0.wireOp",EDGE,"E11.29.8"),sQuery(id+"F0.wireOp",EDGE,"E11.29.9"),sQuery(id+"F0.wireOp",EDGE,"E11.30.0"),sQuery(id+"F0.wireOp",EDGE,"E11.30.1"),sQuery(id+"F0.wireOp",EDGE,"E11.30.2"),sQuery(id+"F0.wireOp",EDGE,"E11.30.3"),sQuery(id+"F0.wireOp",EDGE,"E11.30.4"),sQuery(id+"F0.wireOp",EDGE,"E11.30.5"),sQuery(id+"F0.wireOp",EDGE,"E11.30.6"),sQuery(id+"F0.wireOp",EDGE,"E11.30.7"),sQuery(id+"F0.wireOp",EDGE,"E11.30.8"),sQuery(id+"F0.wireOp",EDGE,"E11.30.9"),sQuery(id+"F0.wireOp",EDGE,"E11.31.0"),sQuery(id+"F0.wireOp",EDGE,"E11.31.1"),sQuery(id+"F0.wireOp",EDGE,"E11.31.2"),sQuery(id+"F0.wireOp",EDGE,"E11.31.3"),sQuery(id+"F0.wireOp",EDGE,"E11.31.4"),sQuery(id+"F0.wireOp",EDGE,"E11.31.5"),sQuery(id+"F0.wireOp",EDGE,"E11.31.6"),sQuery(id+"F0.wireOp",EDGE,"E11.31.7"),sQuery(id+"F0.wireOp",EDGE,"E11.31.8"),sQuery(id+"F0.wireOp",EDGE,"E11.31.9"),sQuery(id+"F0.wireOp",EDGE,"E11.32.0"),sQuery(id+"F0.wireOp",EDGE,"E11.32.1"),sQuery(id+"F0.wireOp",EDGE,"E11.32.2"),sQuery(id+"F0.wireOp",EDGE,"E11.32.3"),sQuery(id+"F0.wireOp",EDGE,"E11.32.4"),sQuery(id+"F0.wireOp",EDGE,"E11.32.5"),sQuery(id+"F0.wireOp",EDGE,"E11.32.6"),sQuery(id+"F0.wireOp",EDGE,"E11.32.7"),sQuery(id+"F0.wireOp",EDGE,"E11.32.8"),sQuery(id+"F0.wireOp",EDGE,"E11.32.9"),sQuery(id+"F0.wireOp",EDGE,"E11.33.0"),sQuery(id+"F0.wireOp",EDGE,"E11.33.1"),sQuery(id+"F0.wireOp",EDGE,"E11.33.2"),sQuery(id+"F0.wireOp",EDGE,"E11.33.3"),sQuery(id+"F0.wireOp",EDGE,"E11.33.4"),sQuery(id+"F0.wireOp",EDGE,"E11.33.5"),sQuery(id+"F0.wireOp",EDGE,"E11.33.6"),sQuery(id+"F0.wireOp",EDGE,"E11.33.7"),sQuery(id+"F0.wireOp",EDGE,"E11.33.8"),sQuery(id+"F0.wireOp",EDGE,"E11.33.9"),sQuery(id+"F0.wireOp",EDGE,"E11.34.0"),sQuery(id+"F0.wireOp",EDGE,"E11.34.1"),sQuery(id+"F0.wireOp",EDGE,"E11.34.2"),sQuery(id+"F0.wireOp",EDGE,"E11.34.3"),sQuery(id+"F0.wireOp",EDGE,"E11.34.4"),sQuery(id+"F0.wireOp",EDGE,"E11.34.5"),sQuery(id+"F0.wireOp",EDGE,"E11.34.6"),sQuery(id+"F0.wireOp",EDGE,"E11.34.7"),sQuery(id+"F0.wireOp",EDGE,"E11.34.8"),sQuery(id+"F0.wireOp",EDGE,"E11.34.9"),sQuery(id+"F0.wireOp",EDGE,"E11.35.0"),sQuery(id+"F0.wireOp",EDGE,"E11.35.1"),sQuery(id+"F0.wireOp",EDGE,"E11.35.2"),sQuery(id+"F0.wireOp",EDGE,"E11.35.3"),sQuery(id+"F0.wireOp",EDGE,"E11.35.4"),sQuery(id+"F0.wireOp",EDGE,"E11.35.5"),sQuery(id+"F0.wireOp",EDGE,"E11.35.6"),sQuery(id+"F0.wireOp",EDGE,"E11.35.7"),sQuery(id+"F0.wireOp",EDGE,"E11.35.8"),sQuery(id+"F0.wireOp",EDGE,"E11.35.9"),sQuery(id+"F0.wireOp",EDGE,"E12"),sQuery(id+"F0.wireOp",EDGE,"E13"),sQuery(id+"F0.wireOp",EDGE,"E14"),sQuery(id+"F0.wireOp",EDGE,"E15"),sQuery(id+"F0.wireOp",EDGE,"E16"),sQuery(id+"F0.wireOp",EDGE,"E17"),sQuery(id+"F0.wireOp",EDGE,"E18"),sQuery(id+"F0.wireOp",EDGE,"E19"),sQuery(id+"F0.wireOp",EDGE,"E20"),sQuery(id+"F0.wireOp",EDGE,"E21"),sQuery(id+"F0.wireOp",EDGE,"E22"),sQuery(id+"F0.wireOp",EDGE,"E23"),sQuery(id+"F0.wireOp",EDGE,"E24"),sQuery(id+"F0.wireOp",EDGE,"E25"),sQuery(id+"F0.wireOp",EDGE,"E26"),sQuery(id+"F0.wireOp",EDGE,"E27"),sQuery(id+"F0.wireOp",EDGE,"E28"),sQuery(id+"F0.wireOp",EDGE,"E29"),sQuery(id+"F0.wireOp",EDGE,"E30"),sQuery(id+"F0.wireOp",EDGE,"E31"),sQuery(id+"F0.wireOp",EDGE,"E32"),sQuery(id+"F0.wireOp",EDGE,"E33"),sQuery(id+"F0.wireOp",EDGE,"E34"),sQuery(id+"F0.wireOp",EDGE,"E35"),sQuery(id+"F0.wireOp",EDGE,"E36"),sQuery(id+"F0.wireOp",EDGE,"E37"),sQuery(id+"F0.wireOp",EDGE,"E38"),sQuery(id+"F0.wireOp",EDGE,"E39"),sQuery(id+"F0.wireOp",EDGE,"E40"),sQuery(id+"F0.wireOp",EDGE,"E41"),sQuery(id+"F0.wireOp",EDGE,"E42"),sQuery(id+"F0.wireOp",EDGE,"E43"),sQuery(id+"F0.wireOp",EDGE,"E44"),sQuery(id+"F0.wireOp",EDGE,"E45"),sQuery(id+"F0.wireOp",EDGE,"E46"),sQuery(id+"F0.wireOp",EDGE,"E47"),sQuery(id+"F0.wireOp",EDGE,"E48"),sQuery(id+"F0.wireOp",EDGE,"E49"),sQuery(id+"F0.wireOp",EDGE,"E50"),sQuery(id+"F0.wireOp",EDGE,"E51"),sQuery(id+"F0.wireOp",EDGE,"E52"),sQuery(id+"F0.wireOp",EDGE,"E53"),sQuery(id+"F0.wireOp",EDGE,"E54"),sQuery(id+"F0.wireOp",EDGE,"E55"),sQuery(id+"F0.wireOp",EDGE,"E56"),sQuery(id+"F0.wireOp",EDGE,"E57"),sQuery(id+"F0.wireOp",EDGE,"E58"),sQuery(id+"F0.wireOp",EDGE,"E59"),sQuery(id+"F0.wireOp",EDGE,"E60"),sQuery(id+"F0.wireOp",EDGE,"E61"),sQuery(id+"F0.wireOp",EDGE,"E62"),sQuery(id+"F0.wireOp",EDGE,"E63"),sQuery(id+"F0.wireOp",EDGE,"E64"),sQuery(id+"F0.wireOp",EDGE,"E65"),sQuery(id+"F0.wireOp",EDGE,"E66"),sQuery(id+"F0.wireOp",EDGE,"E67"),sQuery(id+"F0.wireOp",EDGE,"E68"),sQuery(id+"F0.wireOp",EDGE,"E69"),sQuery(id+"F0.wireOp",EDGE,"E70"),sQuery(id+"F0.wireOp",EDGE,"E71"),sQuery(id+"F0.wireOp",EDGE,"E72"),sQuery(id+"F0.wireOp",EDGE,"E73"),sQuery(id+"F0.wireOp",EDGE,"E74"),sQuery(id+"F0.wireOp",EDGE,"E75"),sQuery(id+"F0.wireOp",EDGE,"E76"),sQuery(id+"F0.wireOp",EDGE,"E77"),sQuery(id+"F0.wireOp",EDGE,"E78"),sQuery(id+"F0.wireOp",EDGE,"E79"),sQuery(id+"F0.wireOp",EDGE,"E80"),sQuery(id+"F0.wireOp",EDGE,"E81"),sQuery(id+"F0.wireOp",EDGE,"E82"),sQuery(id+"F0.wireOp",EDGE,"E83"),sQuery(id+"F0.wireOp",EDGE,"E84"),sQuery(id+"F0.wireOp",EDGE,"E85"),sQuery(id+"F0.wireOp",EDGE,"E86"),sQuery(id+"F0.wireOp",EDGE,"E87"),sQuery(id+"F0.wireOp",EDGE,"E88"),sQuery(id+"F0.wireOp",EDGE,"E89"),sQuery(id+"F0.wireOp",EDGE,"E90"),sQuery(id+"F0.wireOp",EDGE,"E91"),sQuery(id+"F0.wireOp",EDGE,"E92"),sQuery(id+"F0.wireOp",EDGE,"E93"),sQuery(id+"F0.wireOp",EDGE,"E94"),sQuery(id+"F0.wireOp",EDGE,"E95"),sQuery(id+"F0.wireOp",EDGE,"E96"),sQuery(id+"F0.wireOp",EDGE,"E97"),sQuery(id+"F0.wireOp",EDGE,"E98"),sQuery(id+"F0.wireOp",EDGE,"E99"),sQuery(id+"F0.wireOp",EDGE,"E100"),sQuery(id+"F0.wireOp",EDGE,"E101"),sQuery(id+"F0.wireOp",EDGE,"E102"),sQuery(id+"F0.wireOp",EDGE,"E103"),sQuery(id+"F0.wireOp",EDGE,"E104"),sQuery(id+"F0.wireOp",EDGE,"E105"),sQuery(id+"F0.wireOp",EDGE,"E106"),sQuery(id+"F0.wireOp",EDGE,"E107"),sQuery(id+"F0.wireOp",EDGE,"E108"),sQuery(id+"F0.wireOp",EDGE,"E109"),sQuery(id+"F0.wireOp",EDGE,"E110"),sQuery(id+"F0.wireOp",EDGE,"E111"),sQuery(id+"F0.wireOp",EDGE,"E112"),sQuery(id+"F0.wireOp",EDGE,"E113"),sQuery(id+"F0.wireOp",EDGE,"E114"),sQuery(id+"F0.wireOp",EDGE,"E115"),sQuery(id+"F0.wireOp",EDGE,"E116"),sQuery(id+"F0.wireOp",EDGE,"E117"),sQuery(id+"F0.wireOp",EDGE,"E118"),sQuery(id+"F0.wireOp",EDGE,"E119"),sQuery(id+"F0.wireOp",EDGE,"E120"),sQuery(id+"F0.wireOp",EDGE,"E121"),sQuery(id+"F0.wireOp",EDGE,"E122"),sQuery(id+"F0.wireOp",EDGE,"E123"),sQuery(id+"F0.wireOp",EDGE,"E124"),sQuery(id+"F0.wireOp",EDGE,"E125"),sQuery(id+"F0.wireOp",EDGE,"E126"),sQuery(id+"F0.wireOp",EDGE,"E127"),sQuery(id+"F0.wireOp",EDGE,"E128"),sQuery(id+"F0.wireOp",EDGE,"E129"),sQuery(id+"F0.wireOp",EDGE,"E130"),sQuery(id+"F0.wireOp",EDGE,"E131"),sQuery(id+"F0.wireOp",EDGE,"E132"),sQuery(id+"F0.wireOp",EDGE,"E133"),sQuery(id+"F0.wireOp",EDGE,"E134"),sQuery(id+"F0.wireOp",EDGE,"E135"),sQuery(id+"F0.wireOp",EDGE,"E136"),sQuery(id+"F0.wireOp",EDGE,"E137"),sQuery(id+"F0.wireOp",EDGE,"E138"),sQuery(id+"F0.wireOp",EDGE,"E139"),sQuery(id+"F0.wireOp",EDGE,"E140"),sQuery(id+"F0.wireOp",EDGE,"E141"),sQuery(id+"F0.wireOp",EDGE,"E142"),sQuery(id+"F0.wireOp",EDGE,"E143"),sQuery(id+"F0.wireOp",EDGE,"E144"),sQuery(id+"F0.wireOp",EDGE,"E145"),sQuery(id+"F0.wireOp",EDGE,"E146"),sQuery(id+"F0.wireOp",EDGE,"E147"),sQuery(id+"F0.wireOp",EDGE,"E148"),sQuery(id+"F0.wireOp",EDGE,"E149"),sQuery(id+"F0.wireOp",EDGE,"E150"),sQuery(id+"F0.wireOp",EDGE,"E151"),sQuery(id+"F0.wireOp",EDGE,"E152"),sQuery(id+"F0.wireOp",EDGE,"E153"),sQuery(id+"F0.wireOp",EDGE,"E154")])],"isStart":false});
            var sketch = newSketch(context, id + "F2", { "sketchPlane" : qUnion([Q0])});
            skCircle(sketch, "E155", {"center": v(0, 0) * mm, "radius": 3.18 * mm});
            skSolve(sketch);
        }
        {
            var Q0;
            Q0 = qSketchRegion(id + "F2", true);
            extrude(context, id + "F3", {"entities" : qUnion([Q0]), "operationType" : NewBodyOperationType.REMOVE, "endBound" : BoundingType.THROUGH_ALL, "oppositeDirection" : true, "depth" : 25.4 * mm});
        }
        {
            var Q0;
            Q0=makeQuery(id+"F1.opExtrude","CAP_FACE",FACE,{"disambiguationData":[OSD([sQuery(id+"F0.wireOp",EDGE,"E0.trimOffspring"),sQuery(id+"F0.wireOp",EDGE,"E1"),sQuery(id+"F0.wireOp",EDGE,"E2"),sQuery(id+"F0.wireOp",EDGE,"E3.filletArc"),sQuery(id+"F0.wireOp",EDGE,"E4.filletArc"),sQuery(id+"F0.wireOp",EDGE,"E5.filletArc"),sQuery(id+"F0.wireOp",EDGE,"E6.MirrorCS"),sQuery(id+"F0.wireOp",EDGE,"E7.MirrorCS"),sQuery(id+"F0.wireOp",EDGE,"E8.MirrorCS"),sQuery(id+"F0.wireOp",EDGE,"E9.MirrorCS"),sQuery(id+"F0.wireOp",EDGE,"E10.MirrorCS"),sQuery(id+"F0.wireOp",EDGE,"E11.1.0"),sQuery(id+"F0.wireOp",EDGE,"E11.1.1"),sQuery(id+"F0.wireOp",EDGE,"E11.1.2"),sQuery(id+"F0.wireOp",EDGE,"E11.1.3"),sQuery(id+"F0.wireOp",EDGE,"E11.1.4"),sQuery(id+"F0.wireOp",EDGE,"E11.1.5"),sQuery(id+"F0.wireOp",EDGE,"E11.1.6"),sQuery(id+"F0.wireOp",EDGE,"E11.1.7"),sQuery(id+"F0.wireOp",EDGE,"E11.1.8"),sQuery(id+"F0.wireOp",EDGE,"E11.1.9"),sQuery(id+"F0.wireOp",EDGE,"E11.2.0"),sQuery(id+"F0.wireOp",EDGE,"E11.2.1"),sQuery(id+"F0.wireOp",EDGE,"E11.2.2"),sQuery(id+"F0.wireOp",EDGE,"E11.2.3"),sQuery(id+"F0.wireOp",EDGE,"E11.2.4"),sQuery(id+"F0.wireOp",EDGE,"E11.2.5"),sQuery(id+"F0.wireOp",EDGE,"E11.2.6"),sQuery(id+"F0.wireOp",EDGE,"E11.2.7"),sQuery(id+"F0.wireOp",EDGE,"E11.2.8"),sQuery(id+"F0.wireOp",EDGE,"E11.2.9"),sQuery(id+"F0.wireOp",EDGE,"E11.3.0"),sQuery(id+"F0.wireOp",EDGE,"E11.3.1"),sQuery(id+"F0.wireOp",EDGE,"E11.3.2"),sQuery(id+"F0.wireOp",EDGE,"E11.3.3"),sQuery(id+"F0.wireOp",EDGE,"E11.3.4"),sQuery(id+"F0.wireOp",EDGE,"E11.3.5"),sQuery(id+"F0.wireOp",EDGE,"E11.3.6"),sQuery(id+"F0.wireOp",EDGE,"E11.3.7"),sQuery(id+"F0.wireOp",EDGE,"E11.3.8"),sQuery(id+"F0.wireOp",EDGE,"E11.3.9"),sQuery(id+"F0.wireOp",EDGE,"E11.4.0"),sQuery(id+"F0.wireOp",EDGE,"E11.4.1"),sQuery(id+"F0.wireOp",EDGE,"E11.4.2"),sQuery(id+"F0.wireOp",EDGE,"E11.4.3"),sQuery(id+"F0.wireOp",EDGE,"E11.4.4"),sQuery(id+"F0.wireOp",EDGE,"E11.4.5"),sQuery(id+"F0.wireOp",EDGE,"E11.4.6"),sQuery(id+"F0.wireOp",EDGE,"E11.4.7"),sQuery(id+"F0.wireOp",EDGE,"E11.4.8"),sQuery(id+"F0.wireOp",EDGE,"E11.4.9"),sQuery(id+"F0.wireOp",EDGE,"E11.5.0"),sQuery(id+"F0.wireOp",EDGE,"E11.5.1"),sQuery(id+"F0.wireOp",EDGE,"E11.5.2"),sQuery(id+"F0.wireOp",EDGE,"E11.5.3"),sQuery(id+"F0.wireOp",EDGE,"E11.5.4"),sQuery(id+"F0.wireOp",EDGE,"E11.5.5"),sQuery(id+"F0.wireOp",EDGE,"E11.5.6"),sQuery(id+"F0.wireOp",EDGE,"E11.5.7"),sQuery(id+"F0.wireOp",EDGE,"E11.5.8"),sQuery(id+"F0.wireOp",EDGE,"E11.5.9"),sQuery(id+"F0.wireOp",EDGE,"E11.6.0"),sQuery(id+"F0.wireOp",EDGE,"E11.6.1"),sQuery(id+"F0.wireOp",EDGE,"E11.6.2"),sQuery(id+"F0.wireOp",EDGE,"E11.6.3"),sQuery(id+"F0.wireOp",EDGE,"E11.6.4"),sQuery(id+"F0.wireOp",EDGE,"E11.6.5"),sQuery(id+"F0.wireOp",EDGE,"E11.6.6"),sQuery(id+"F0.wireOp",EDGE,"E11.6.7"),sQuery(id+"F0.wireOp",EDGE,"E11.6.8"),sQuery(id+"F0.wireOp",EDGE,"E11.6.9"),sQuery(id+"F0.wireOp",EDGE,"E11.7.0"),sQuery(id+"F0.wireOp",EDGE,"E11.7.1"),sQuery(id+"F0.wireOp",EDGE,"E11.7.2"),sQuery(id+"F0.wireOp",EDGE,"E11.7.3"),sQuery(id+"F0.wireOp",EDGE,"E11.7.4"),sQuery(id+"F0.wireOp",EDGE,"E11.7.5"),sQuery(id+"F0.wireOp",EDGE,"E11.7.6"),sQuery(id+"F0.wireOp",EDGE,"E11.7.7"),sQuery(id+"F0.wireOp",EDGE,"E11.7.8"),sQuery(id+"F0.wireOp",EDGE,"E11.7.9"),sQuery(id+"F0.wireOp",EDGE,"E11.8.0"),sQuery(id+"F0.wireOp",EDGE,"E11.8.1"),sQuery(id+"F0.wireOp",EDGE,"E11.8.2"),sQuery(id+"F0.wireOp",EDGE,"E11.8.3"),sQuery(id+"F0.wireOp",EDGE,"E11.8.4"),sQuery(id+"F0.wireOp",EDGE,"E11.8.5"),sQuery(id+"F0.wireOp",EDGE,"E11.8.6"),sQuery(id+"F0.wireOp",EDGE,"E11.8.7"),sQuery(id+"F0.wireOp",EDGE,"E11.8.8"),sQuery(id+"F0.wireOp",EDGE,"E11.8.9"),sQuery(id+"F0.wireOp",EDGE,"E11.9.0"),sQuery(id+"F0.wireOp",EDGE,"E11.9.1"),sQuery(id+"F0.wireOp",EDGE,"E11.9.2"),sQuery(id+"F0.wireOp",EDGE,"E11.9.3"),sQuery(id+"F0.wireOp",EDGE,"E11.9.4"),sQuery(id+"F0.wireOp",EDGE,"E11.9.5"),sQuery(id+"F0.wireOp",EDGE,"E11.9.6"),sQuery(id+"F0.wireOp",EDGE,"E11.9.7"),sQuery(id+"F0.wireOp",EDGE,"E11.9.8"),sQuery(id+"F0.wireOp",EDGE,"E11.9.9"),sQuery(id+"F0.wireOp",EDGE,"E11.10.0"),sQuery(id+"F0.wireOp",EDGE,"E11.10.1"),sQuery(id+"F0.wireOp",EDGE,"E11.10.2"),sQuery(id+"F0.wireOp",EDGE,"E11.10.3"),sQuery(id+"F0.wireOp",EDGE,"E11.10.4"),sQuery(id+"F0.wireOp",EDGE,"E11.10.5"),sQuery(id+"F0.wireOp",EDGE,"E11.10.6"),sQuery(id+"F0.wireOp",EDGE,"E11.10.7"),sQuery(id+"F0.wireOp",EDGE,"E11.10.8"),sQuery(id+"F0.wireOp",EDGE,"E11.10.9"),sQuery(id+"F0.wireOp",EDGE,"E11.11.0"),sQuery(id+"F0.wireOp",EDGE,"E11.11.1"),sQuery(id+"F0.wireOp",EDGE,"E11.11.2"),sQuery(id+"F0.wireOp",EDGE,"E11.11.3"),sQuery(id+"F0.wireOp",EDGE,"E11.11.4"),sQuery(id+"F0.wireOp",EDGE,"E11.11.5"),sQuery(id+"F0.wireOp",EDGE,"E11.11.6"),sQuery(id+"F0.wireOp",EDGE,"E11.11.7"),sQuery(id+"F0.wireOp",EDGE,"E11.11.8"),sQuery(id+"F0.wireOp",EDGE,"E11.11.9"),sQuery(id+"F0.wireOp",EDGE,"E11.12.0"),sQuery(id+"F0.wireOp",EDGE,"E11.12.1"),sQuery(id+"F0.wireOp",EDGE,"E11.12.2"),sQuery(id+"F0.wireOp",EDGE,"E11.12.3"),sQuery(id+"F0.wireOp",EDGE,"E11.12.4"),sQuery(id+"F0.wireOp",EDGE,"E11.12.5"),sQuery(id+"F0.wireOp",EDGE,"E11.12.6"),sQuery(id+"F0.wireOp",EDGE,"E11.12.7"),sQuery(id+"F0.wireOp",EDGE,"E11.12.8"),sQuery(id+"F0.wireOp",EDGE,"E11.12.9"),sQuery(id+"F0.wireOp",EDGE,"E11.13.0"),sQuery(id+"F0.wireOp",EDGE,"E11.13.1"),sQuery(id+"F0.wireOp",EDGE,"E11.13.2"),sQuery(id+"F0.wireOp",EDGE,"E11.13.3"),sQuery(id+"F0.wireOp",EDGE,"E11.13.4"),sQuery(id+"F0.wireOp",EDGE,"E11.13.5"),sQuery(id+"F0.wireOp",EDGE,"E11.13.6"),sQuery(id+"F0.wireOp",EDGE,"E11.13.7"),sQuery(id+"F0.wireOp",EDGE,"E11.13.8"),sQuery(id+"F0.wireOp",EDGE,"E11.13.9"),sQuery(id+"F0.wireOp",EDGE,"E11.14.0"),sQuery(id+"F0.wireOp",EDGE,"E11.14.1"),sQuery(id+"F0.wireOp",EDGE,"E11.14.2"),sQuery(id+"F0.wireOp",EDGE,"E11.14.3"),sQuery(id+"F0.wireOp",EDGE,"E11.14.4"),sQuery(id+"F0.wireOp",EDGE,"E11.14.5"),sQuery(id+"F0.wireOp",EDGE,"E11.14.6"),sQuery(id+"F0.wireOp",EDGE,"E11.14.7"),sQuery(id+"F0.wireOp",EDGE,"E11.14.8"),sQuery(id+"F0.wireOp",EDGE,"E11.14.9"),sQuery(id+"F0.wireOp",EDGE,"E11.15.0"),sQuery(id+"F0.wireOp",EDGE,"E11.15.1"),sQuery(id+"F0.wireOp",EDGE,"E11.15.2"),sQuery(id+"F0.wireOp",EDGE,"E11.15.3"),sQuery(id+"F0.wireOp",EDGE,"E11.15.4"),sQuery(id+"F0.wireOp",EDGE,"E11.15.5"),sQuery(id+"F0.wireOp",EDGE,"E11.15.6"),sQuery(id+"F0.wireOp",EDGE,"E11.15.7"),sQuery(id+"F0.wireOp",EDGE,"E11.15.8"),sQuery(id+"F0.wireOp",EDGE,"E11.15.9"),sQuery(id+"F0.wireOp",EDGE,"E11.16.0"),sQuery(id+"F0.wireOp",EDGE,"E11.16.1"),sQuery(id+"F0.wireOp",EDGE,"E11.16.2"),sQuery(id+"F0.wireOp",EDGE,"E11.16.3"),sQuery(id+"F0.wireOp",EDGE,"E11.16.4"),sQuery(id+"F0.wireOp",EDGE,"E11.16.5"),sQuery(id+"F0.wireOp",EDGE,"E11.16.6"),sQuery(id+"F0.wireOp",EDGE,"E11.16.7"),sQuery(id+"F0.wireOp",EDGE,"E11.16.8"),sQuery(id+"F0.wireOp",EDGE,"E11.16.9"),sQuery(id+"F0.wireOp",EDGE,"E11.17.0"),sQuery(id+"F0.wireOp",EDGE,"E11.17.1"),sQuery(id+"F0.wireOp",EDGE,"E11.17.2"),sQuery(id+"F0.wireOp",EDGE,"E11.17.3"),sQuery(id+"F0.wireOp",EDGE,"E11.17.4"),sQuery(id+"F0.wireOp",EDGE,"E11.17.5"),sQuery(id+"F0.wireOp",EDGE,"E11.17.6"),sQuery(id+"F0.wireOp",EDGE,"E11.17.7"),sQuery(id+"F0.wireOp",EDGE,"E11.17.8"),sQuery(id+"F0.wireOp",EDGE,"E11.17.9"),sQuery(id+"F0.wireOp",EDGE,"E11.18.0"),sQuery(id+"F0.wireOp",EDGE,"E11.18.1"),sQuery(id+"F0.wireOp",EDGE,"E11.18.2"),sQuery(id+"F0.wireOp",EDGE,"E11.18.3"),sQuery(id+"F0.wireOp",EDGE,"E11.18.4"),sQuery(id+"F0.wireOp",EDGE,"E11.18.5"),sQuery(id+"F0.wireOp",EDGE,"E11.18.6"),sQuery(id+"F0.wireOp",EDGE,"E11.18.7"),sQuery(id+"F0.wireOp",EDGE,"E11.18.8"),sQuery(id+"F0.wireOp",EDGE,"E11.18.9"),sQuery(id+"F0.wireOp",EDGE,"E11.19.0"),sQuery(id+"F0.wireOp",EDGE,"E11.19.1"),sQuery(id+"F0.wireOp",EDGE,"E11.19.2"),sQuery(id+"F0.wireOp",EDGE,"E11.19.3"),sQuery(id+"F0.wireOp",EDGE,"E11.19.4"),sQuery(id+"F0.wireOp",EDGE,"E11.19.5"),sQuery(id+"F0.wireOp",EDGE,"E11.19.6"),sQuery(id+"F0.wireOp",EDGE,"E11.19.7"),sQuery(id+"F0.wireOp",EDGE,"E11.19.8"),sQuery(id+"F0.wireOp",EDGE,"E11.19.9"),sQuery(id+"F0.wireOp",EDGE,"E11.20.0"),sQuery(id+"F0.wireOp",EDGE,"E11.20.1"),sQuery(id+"F0.wireOp",EDGE,"E11.20.2"),sQuery(id+"F0.wireOp",EDGE,"E11.20.3"),sQuery(id+"F0.wireOp",EDGE,"E11.20.4"),sQuery(id+"F0.wireOp",EDGE,"E11.20.5"),sQuery(id+"F0.wireOp",EDGE,"E11.20.6"),sQuery(id+"F0.wireOp",EDGE,"E11.20.7"),sQuery(id+"F0.wireOp",EDGE,"E11.20.8"),sQuery(id+"F0.wireOp",EDGE,"E11.20.9"),sQuery(id+"F0.wireOp",EDGE,"E11.21.0"),sQuery(id+"F0.wireOp",EDGE,"E11.21.1"),sQuery(id+"F0.wireOp",EDGE,"E11.21.2"),sQuery(id+"F0.wireOp",EDGE,"E11.21.3"),sQuery(id+"F0.wireOp",EDGE,"E11.21.4"),sQuery(id+"F0.wireOp",EDGE,"E11.21.5"),sQuery(id+"F0.wireOp",EDGE,"E11.21.6"),sQuery(id+"F0.wireOp",EDGE,"E11.21.7"),sQuery(id+"F0.wireOp",EDGE,"E11.21.8"),sQuery(id+"F0.wireOp",EDGE,"E11.21.9"),sQuery(id+"F0.wireOp",EDGE,"E11.22.0"),sQuery(id+"F0.wireOp",EDGE,"E11.22.1"),sQuery(id+"F0.wireOp",EDGE,"E11.22.2"),sQuery(id+"F0.wireOp",EDGE,"E11.22.3"),sQuery(id+"F0.wireOp",EDGE,"E11.22.4"),sQuery(id+"F0.wireOp",EDGE,"E11.22.5"),sQuery(id+"F0.wireOp",EDGE,"E11.22.6"),sQuery(id+"F0.wireOp",EDGE,"E11.22.7"),sQuery(id+"F0.wireOp",EDGE,"E11.22.8"),sQuery(id+"F0.wireOp",EDGE,"E11.22.9"),sQuery(id+"F0.wireOp",EDGE,"E11.23.0"),sQuery(id+"F0.wireOp",EDGE,"E11.23.1"),sQuery(id+"F0.wireOp",EDGE,"E11.23.2"),sQuery(id+"F0.wireOp",EDGE,"E11.23.3"),sQuery(id+"F0.wireOp",EDGE,"E11.23.4"),sQuery(id+"F0.wireOp",EDGE,"E11.23.5"),sQuery(id+"F0.wireOp",EDGE,"E11.23.6"),sQuery(id+"F0.wireOp",EDGE,"E11.23.7"),sQuery(id+"F0.wireOp",EDGE,"E11.23.8"),sQuery(id+"F0.wireOp",EDGE,"E11.23.9"),sQuery(id+"F0.wireOp",EDGE,"E11.24.0"),sQuery(id+"F0.wireOp",EDGE,"E11.24.1"),sQuery(id+"F0.wireOp",EDGE,"E11.24.2"),sQuery(id+"F0.wireOp",EDGE,"E11.24.3"),sQuery(id+"F0.wireOp",EDGE,"E11.24.4"),sQuery(id+"F0.wireOp",EDGE,"E11.24.5"),sQuery(id+"F0.wireOp",EDGE,"E11.24.6"),sQuery(id+"F0.wireOp",EDGE,"E11.24.7"),sQuery(id+"F0.wireOp",EDGE,"E11.24.8"),sQuery(id+"F0.wireOp",EDGE,"E11.24.9"),sQuery(id+"F0.wireOp",EDGE,"E11.25.0"),sQuery(id+"F0.wireOp",EDGE,"E11.25.1"),sQuery(id+"F0.wireOp",EDGE,"E11.25.2"),sQuery(id+"F0.wireOp",EDGE,"E11.25.3"),sQuery(id+"F0.wireOp",EDGE,"E11.25.4"),sQuery(id+"F0.wireOp",EDGE,"E11.25.5"),sQuery(id+"F0.wireOp",EDGE,"E11.25.6"),sQuery(id+"F0.wireOp",EDGE,"E11.25.7"),sQuery(id+"F0.wireOp",EDGE,"E11.25.8"),sQuery(id+"F0.wireOp",EDGE,"E11.25.9"),sQuery(id+"F0.wireOp",EDGE,"E11.26.0"),sQuery(id+"F0.wireOp",EDGE,"E11.26.1"),sQuery(id+"F0.wireOp",EDGE,"E11.26.2"),sQuery(id+"F0.wireOp",EDGE,"E11.26.3"),sQuery(id+"F0.wireOp",EDGE,"E11.26.4"),sQuery(id+"F0.wireOp",EDGE,"E11.26.5"),sQuery(id+"F0.wireOp",EDGE,"E11.26.6"),sQuery(id+"F0.wireOp",EDGE,"E11.26.7"),sQuery(id+"F0.wireOp",EDGE,"E11.26.8"),sQuery(id+"F0.wireOp",EDGE,"E11.26.9"),sQuery(id+"F0.wireOp",EDGE,"E11.27.0"),sQuery(id+"F0.wireOp",EDGE,"E11.27.1"),sQuery(id+"F0.wireOp",EDGE,"E11.27.2"),sQuery(id+"F0.wireOp",EDGE,"E11.27.3"),sQuery(id+"F0.wireOp",EDGE,"E11.27.4"),sQuery(id+"F0.wireOp",EDGE,"E11.27.5"),sQuery(id+"F0.wireOp",EDGE,"E11.27.6"),sQuery(id+"F0.wireOp",EDGE,"E11.27.7"),sQuery(id+"F0.wireOp",EDGE,"E11.27.8"),sQuery(id+"F0.wireOp",EDGE,"E11.27.9"),sQuery(id+"F0.wireOp",EDGE,"E11.28.0"),sQuery(id+"F0.wireOp",EDGE,"E11.28.1"),sQuery(id+"F0.wireOp",EDGE,"E11.28.2"),sQuery(id+"F0.wireOp",EDGE,"E11.28.3"),sQuery(id+"F0.wireOp",EDGE,"E11.28.4"),sQuery(id+"F0.wireOp",EDGE,"E11.28.5"),sQuery(id+"F0.wireOp",EDGE,"E11.28.6"),sQuery(id+"F0.wireOp",EDGE,"E11.28.7"),sQuery(id+"F0.wireOp",EDGE,"E11.28.8"),sQuery(id+"F0.wireOp",EDGE,"E11.28.9"),sQuery(id+"F0.wireOp",EDGE,"E11.29.0"),sQuery(id+"F0.wireOp",EDGE,"E11.29.1"),sQuery(id+"F0.wireOp",EDGE,"E11.29.2"),sQuery(id+"F0.wireOp",EDGE,"E11.29.3"),sQuery(id+"F0.wireOp",EDGE,"E11.29.4"),sQuery(id+"F0.wireOp",EDGE,"E11.29.5"),sQuery(id+"F0.wireOp",EDGE,"E11.29.6"),sQuery(id+"F0.wireOp",EDGE,"E11.29.7"),sQuery(id+"F0.wireOp",EDGE,"E11.29.8"),sQuery(id+"F0.wireOp",EDGE,"E11.29.9"),sQuery(id+"F0.wireOp",EDGE,"E11.30.0"),sQuery(id+"F0.wireOp",EDGE,"E11.30.1"),sQuery(id+"F0.wireOp",EDGE,"E11.30.2"),sQuery(id+"F0.wireOp",EDGE,"E11.30.3"),sQuery(id+"F0.wireOp",EDGE,"E11.30.4"),sQuery(id+"F0.wireOp",EDGE,"E11.30.5"),sQuery(id+"F0.wireOp",EDGE,"E11.30.6"),sQuery(id+"F0.wireOp",EDGE,"E11.30.7"),sQuery(id+"F0.wireOp",EDGE,"E11.30.8"),sQuery(id+"F0.wireOp",EDGE,"E11.30.9"),sQuery(id+"F0.wireOp",EDGE,"E11.31.0"),sQuery(id+"F0.wireOp",EDGE,"E11.31.1"),sQuery(id+"F0.wireOp",EDGE,"E11.31.2"),sQuery(id+"F0.wireOp",EDGE,"E11.31.3"),sQuery(id+"F0.wireOp",EDGE,"E11.31.4"),sQuery(id+"F0.wireOp",EDGE,"E11.31.5"),sQuery(id+"F0.wireOp",EDGE,"E11.31.6"),sQuery(id+"F0.wireOp",EDGE,"E11.31.7"),sQuery(id+"F0.wireOp",EDGE,"E11.31.8"),sQuery(id+"F0.wireOp",EDGE,"E11.31.9"),sQuery(id+"F0.wireOp",EDGE,"E11.32.0"),sQuery(id+"F0.wireOp",EDGE,"E11.32.1"),sQuery(id+"F0.wireOp",EDGE,"E11.32.2"),sQuery(id+"F0.wireOp",EDGE,"E11.32.3"),sQuery(id+"F0.wireOp",EDGE,"E11.32.4"),sQuery(id+"F0.wireOp",EDGE,"E11.32.5"),sQuery(id+"F0.wireOp",EDGE,"E11.32.6"),sQuery(id+"F0.wireOp",EDGE,"E11.32.7"),sQuery(id+"F0.wireOp",EDGE,"E11.32.8"),sQuery(id+"F0.wireOp",EDGE,"E11.32.9"),sQuery(id+"F0.wireOp",EDGE,"E11.33.0"),sQuery(id+"F0.wireOp",EDGE,"E11.33.1"),sQuery(id+"F0.wireOp",EDGE,"E11.33.2"),sQuery(id+"F0.wireOp",EDGE,"E11.33.3"),sQuery(id+"F0.wireOp",EDGE,"E11.33.4"),sQuery(id+"F0.wireOp",EDGE,"E11.33.5"),sQuery(id+"F0.wireOp",EDGE,"E11.33.6"),sQuery(id+"F0.wireOp",EDGE,"E11.33.7"),sQuery(id+"F0.wireOp",EDGE,"E11.33.8"),sQuery(id+"F0.wireOp",EDGE,"E11.33.9"),sQuery(id+"F0.wireOp",EDGE,"E11.34.0"),sQuery(id+"F0.wireOp",EDGE,"E11.34.1"),sQuery(id+"F0.wireOp",EDGE,"E11.34.2"),sQuery(id+"F0.wireOp",EDGE,"E11.34.3"),sQuery(id+"F0.wireOp",EDGE,"E11.34.4"),sQuery(id+"F0.wireOp",EDGE,"E11.34.5"),sQuery(id+"F0.wireOp",EDGE,"E11.34.6"),sQuery(id+"F0.wireOp",EDGE,"E11.34.7"),sQuery(id+"F0.wireOp",EDGE,"E11.34.8"),sQuery(id+"F0.wireOp",EDGE,"E11.34.9"),sQuery(id+"F0.wireOp",EDGE,"E11.35.0"),sQuery(id+"F0.wireOp",EDGE,"E11.35.1"),sQuery(id+"F0.wireOp",EDGE,"E11.35.2"),sQuery(id+"F0.wireOp",EDGE,"E11.35.3"),sQuery(id+"F0.wireOp",EDGE,"E11.35.4"),sQuery(id+"F0.wireOp",EDGE,"E11.35.5"),sQuery(id+"F0.wireOp",EDGE,"E11.35.6"),sQuery(id+"F0.wireOp",EDGE,"E11.35.7"),sQuery(id+"F0.wireOp",EDGE,"E11.35.8"),sQuery(id+"F0.wireOp",EDGE,"E11.35.9"),sQuery(id+"F0.wireOp",EDGE,"E12"),sQuery(id+"F0.wireOp",EDGE,"E13"),sQuery(id+"F0.wireOp",EDGE,"E14"),sQuery(id+"F0.wireOp",EDGE,"E15"),sQuery(id+"F0.wireOp",EDGE,"E16"),sQuery(id+"F0.wireOp",EDGE,"E17"),sQuery(id+"F0.wireOp",EDGE,"E18"),sQuery(id+"F0.wireOp",EDGE,"E19"),sQuery(id+"F0.wireOp",EDGE,"E20"),sQuery(id+"F0.wireOp",EDGE,"E21"),sQuery(id+"F0.wireOp",EDGE,"E22"),sQuery(id+"F0.wireOp",EDGE,"E23"),sQuery(id+"F0.wireOp",EDGE,"E24"),sQuery(id+"F0.wireOp",EDGE,"E25"),sQuery(id+"F0.wireOp",EDGE,"E26"),sQuery(id+"F0.wireOp",EDGE,"E27"),sQuery(id+"F0.wireOp",EDGE,"E28"),sQuery(id+"F0.wireOp",EDGE,"E29"),sQuery(id+"F0.wireOp",EDGE,"E30"),sQuery(id+"F0.wireOp",EDGE,"E31"),sQuery(id+"F0.wireOp",EDGE,"E32"),sQuery(id+"F0.wireOp",EDGE,"E33"),sQuery(id+"F0.wireOp",EDGE,"E34"),sQuery(id+"F0.wireOp",EDGE,"E35"),sQuery(id+"F0.wireOp",EDGE,"E36"),sQuery(id+"F0.wireOp",EDGE,"E37"),sQuery(id+"F0.wireOp",EDGE,"E38"),sQuery(id+"F0.wireOp",EDGE,"E39"),sQuery(id+"F0.wireOp",EDGE,"E40"),sQuery(id+"F0.wireOp",EDGE,"E41"),sQuery(id+"F0.wireOp",EDGE,"E42"),sQuery(id+"F0.wireOp",EDGE,"E43"),sQuery(id+"F0.wireOp",EDGE,"E44"),sQuery(id+"F0.wireOp",EDGE,"E45"),sQuery(id+"F0.wireOp",EDGE,"E46"),sQuery(id+"F0.wireOp",EDGE,"E47"),sQuery(id+"F0.wireOp",EDGE,"E48"),sQuery(id+"F0.wireOp",EDGE,"E49"),sQuery(id+"F0.wireOp",EDGE,"E50"),sQuery(id+"F0.wireOp",EDGE,"E51"),sQuery(id+"F0.wireOp",EDGE,"E52"),sQuery(id+"F0.wireOp",EDGE,"E53"),sQuery(id+"F0.wireOp",EDGE,"E54"),sQuery(id+"F0.wireOp",EDGE,"E55"),sQuery(id+"F0.wireOp",EDGE,"E56"),sQuery(id+"F0.wireOp",EDGE,"E57"),sQuery(id+"F0.wireOp",EDGE,"E58"),sQuery(id+"F0.wireOp",EDGE,"E59"),sQuery(id+"F0.wireOp",EDGE,"E60"),sQuery(id+"F0.wireOp",EDGE,"E61"),sQuery(id+"F0.wireOp",EDGE,"E62"),sQuery(id+"F0.wireOp",EDGE,"E63"),sQuery(id+"F0.wireOp",EDGE,"E64"),sQuery(id+"F0.wireOp",EDGE,"E65"),sQuery(id+"F0.wireOp",EDGE,"E66"),sQuery(id+"F0.wireOp",EDGE,"E67"),sQuery(id+"F0.wireOp",EDGE,"E68"),sQuery(id+"F0.wireOp",EDGE,"E69"),sQuery(id+"F0.wireOp",EDGE,"E70"),sQuery(id+"F0.wireOp",EDGE,"E71"),sQuery(id+"F0.wireOp",EDGE,"E72"),sQuery(id+"F0.wireOp",EDGE,"E73"),sQuery(id+"F0.wireOp",EDGE,"E74"),sQuery(id+"F0.wireOp",EDGE,"E75"),sQuery(id+"F0.wireOp",EDGE,"E76"),sQuery(id+"F0.wireOp",EDGE,"E77"),sQuery(id+"F0.wireOp",EDGE,"E78"),sQuery(id+"F0.wireOp",EDGE,"E79"),sQuery(id+"F0.wireOp",EDGE,"E80"),sQuery(id+"F0.wireOp",EDGE,"E81"),sQuery(id+"F0.wireOp",EDGE,"E82"),sQuery(id+"F0.wireOp",EDGE,"E83"),sQuery(id+"F0.wireOp",EDGE,"E84"),sQuery(id+"F0.wireOp",EDGE,"E85"),sQuery(id+"F0.wireOp",EDGE,"E86"),sQuery(id+"F0.wireOp",EDGE,"E87"),sQuery(id+"F0.wireOp",EDGE,"E88"),sQuery(id+"F0.wireOp",EDGE,"E89"),sQuery(id+"F0.wireOp",EDGE,"E90"),sQuery(id+"F0.wireOp",EDGE,"E91"),sQuery(id+"F0.wireOp",EDGE,"E92"),sQuery(id+"F0.wireOp",EDGE,"E93"),sQuery(id+"F0.wireOp",EDGE,"E94"),sQuery(id+"F0.wireOp",EDGE,"E95"),sQuery(id+"F0.wireOp",EDGE,"E96"),sQuery(id+"F0.wireOp",EDGE,"E97"),sQuery(id+"F0.wireOp",EDGE,"E98"),sQuery(id+"F0.wireOp",EDGE,"E99"),sQuery(id+"F0.wireOp",EDGE,"E100"),sQuery(id+"F0.wireOp",EDGE,"E101"),sQuery(id+"F0.wireOp",EDGE,"E102"),sQuery(id+"F0.wireOp",EDGE,"E103"),sQuery(id+"F0.wireOp",EDGE,"E104"),sQuery(id+"F0.wireOp",EDGE,"E105"),sQuery(id+"F0.wireOp",EDGE,"E106"),sQuery(id+"F0.wireOp",EDGE,"E107"),sQuery(id+"F0.wireOp",EDGE,"E108"),sQuery(id+"F0.wireOp",EDGE,"E109"),sQuery(id+"F0.wireOp",EDGE,"E110"),sQuery(id+"F0.wireOp",EDGE,"E111"),sQuery(id+"F0.wireOp",EDGE,"E112"),sQuery(id+"F0.wireOp",EDGE,"E113"),sQuery(id+"F0.wireOp",EDGE,"E114"),sQuery(id+"F0.wireOp",EDGE,"E115"),sQuery(id+"F0.wireOp",EDGE,"E116"),sQuery(id+"F0.wireOp",EDGE,"E117"),sQuery(id+"F0.wireOp",EDGE,"E118"),sQuery(id+"F0.wireOp",EDGE,"E119"),sQuery(id+"F0.wireOp",EDGE,"E120"),sQuery(id+"F0.wireOp",EDGE,"E121"),sQuery(id+"F0.wireOp",EDGE,"E122"),sQuery(id+"F0.wireOp",EDGE,"E123"),sQuery(id+"F0.wireOp",EDGE,"E124"),sQuery(id+"F0.wireOp",EDGE,"E125"),sQuery(id+"F0.wireOp",EDGE,"E126"),sQuery(id+"F0.wireOp",EDGE,"E127"),sQuery(id+"F0.wireOp",EDGE,"E128"),sQuery(id+"F0.wireOp",EDGE,"E129"),sQuery(id+"F0.wireOp",EDGE,"E130"),sQuery(id+"F0.wireOp",EDGE,"E131"),sQuery(id+"F0.wireOp",EDGE,"E132"),sQuery(id+"F0.wireOp",EDGE,"E133"),sQuery(id+"F0.wireOp",EDGE,"E134"),sQuery(id+"F0.wireOp",EDGE,"E135"),sQuery(id+"F0.wireOp",EDGE,"E136"),sQuery(id+"F0.wireOp",EDGE,"E137"),sQuery(id+"F0.wireOp",EDGE,"E138"),sQuery(id+"F0.wireOp",EDGE,"E139"),sQuery(id+"F0.wireOp",EDGE,"E140"),sQuery(id+"F0.wireOp",EDGE,"E141"),sQuery(id+"F0.wireOp",EDGE,"E142"),sQuery(id+"F0.wireOp",EDGE,"E143"),sQuery(id+"F0.wireOp",EDGE,"E144"),sQuery(id+"F0.wireOp",EDGE,"E145"),sQuery(id+"F0.wireOp",EDGE,"E146"),sQuery(id+"F0.wireOp",EDGE,"E147"),sQuery(id+"F0.wireOp",EDGE,"E148"),sQuery(id+"F0.wireOp",EDGE,"E149"),sQuery(id+"F0.wireOp",EDGE,"E150"),sQuery(id+"F0.wireOp",EDGE,"E151"),sQuery(id+"F0.wireOp",EDGE,"E152"),sQuery(id+"F0.wireOp",EDGE,"E153"),sQuery(id+"F0.wireOp",EDGE,"E154")])],"isStart":false});
            shell(context, id + "F4", {"entities" : qUnion([Q0]), "thickness" : 6.35 * mm});
        }
        {
            var Q0;
            Q0=qCreatedBy(makeId("Right.planeOp"),FACE);
            cPlane(context, id + "F5", {"entities" : qUnion([Q0]), "cplaneType" : CPlaneType.OFFSET, "offset" : 9.52 * mm, "width" : 152.4 * mm, "height" : 152.4 * mm});
        }
        {
            var Q0;
            Q0=qCreatedBy(id+"F5.planeOp",FACE);
            var sketch = newSketch(context, id + "F6", { "sketchPlane" : qUnion([Q0])});
            skCircle(sketch, "E156", {"center": v(-8.4, 0) * mm, "radius": 1.13 * mm});
            skSolve(sketch);
        }
        {
            var Q0;
            Q0=makeQuery(id+"F6.imprint","IMPRINT",FACE,{"disambiguationData":[TD([[makeQuery(id+"F6.imprint","IMPRINT",EDGE,{"derivedFrom":sQuery(id+"F6.wireOp",EDGE,"E156")}),1.0]])]});
            extrude(context, id + "F7", {"entities" : qUnion([Q0]), "operationType" : NewBodyOperationType.REMOVE, "oppositeDirection" : true, "depth" : 9.52 * mm});
        }
    });
